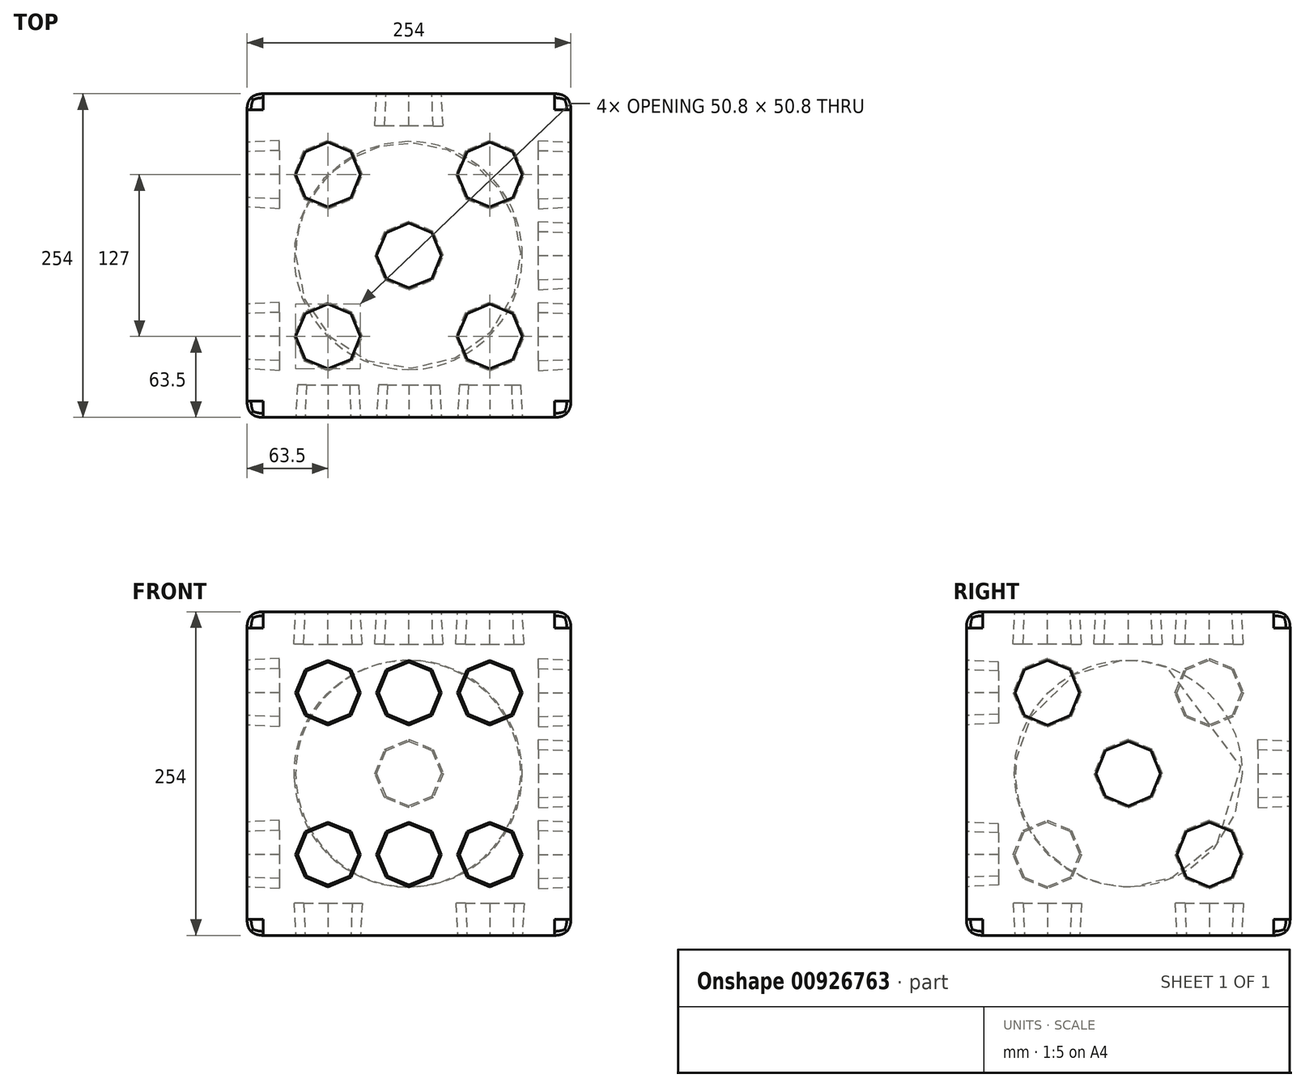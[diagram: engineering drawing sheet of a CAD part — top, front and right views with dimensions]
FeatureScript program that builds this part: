
annotation { "Feature Type Name" : "Feature", "Feature Type Description" : "" }
export const myFeature = defineFeature(function(context is Context, id is Id, definition is map)
    precondition{}
    {
        {
            var Q0;
            Q0=qCreatedBy(makeId("Front.planeOp"),FACE);
            var sketch = newSketch(context, id + "F0", { "sketchPlane" : qUnion([Q0])});
            skLineSegment(sketch, "E0.bottom", {"start": v(127, -127) * mm, "end": v(-127, -127) * mm});
            skLineSegment(sketch, "E0.top", {"start": v(127, 127) * mm, "end": v(-127, 127) * mm});
            skLineSegment(sketch, "E0.left", {"start": v(127, -127) * mm, "end": v(127, 127) * mm});
            skLineSegment(sketch, "E0.right", {"start": v(-127, -127) * mm, "end": v(-127, 127) * mm});
            skPoint(sketch, "E0.middle", {"position": v(0, 0) * mm});
            skLineSegment(sketch, "E1", {"start": v(-63.5, 127) * mm, "end": v(-63.5, -127) * mm, "construction": true});
            skLineSegment(sketch, "E2", {"start": v(0, -127) * mm, "end": v(0, 127) * mm, "construction": true});
            skLineSegment(sketch, "E3", {"start": v(63.5, 127) * mm, "end": v(63.5, -127) * mm, "construction": true});
            skLineSegment(sketch, "E4", {"start": v(-127, 63.5) * mm, "end": v(127, 63.5) * mm, "construction": true});
            skLineSegment(sketch, "E5", {"start": v(-127, 0) * mm, "end": v(127, 0) * mm, "construction": true});
            skLineSegment(sketch, "E6", {"start": v(-127, -63.5) * mm, "end": v(127, -63.5) * mm, "construction": true});
            skLineSegment(sketch, "E7.bottom", {"start": v(-38.1, 38.1) * mm, "end": v(-88.9, 38.1) * mm});
            skLineSegment(sketch, "E7.top", {"start": v(-38.1, 88.9) * mm, "end": v(-88.9, 88.9) * mm});
            skLineSegment(sketch, "E7.left", {"start": v(-38.1, 38.1) * mm, "end": v(-38.1, 88.9) * mm});
            skLineSegment(sketch, "E7.right", {"start": v(-88.9, 38.1) * mm, "end": v(-88.9, 88.9) * mm});
            skPoint(sketch, "E7.middle", {"position": v(-63.5, 63.5) * mm});
            skLineSegment(sketch, "E8.bottom", {"start": v(25.4, 38.1) * mm, "end": v(-25.4, 38.1) * mm});
            skLineSegment(sketch, "E8.top", {"start": v(25.4, 88.9) * mm, "end": v(-25.4, 88.9) * mm});
            skLineSegment(sketch, "E8.left", {"start": v(25.4, 38.1) * mm, "end": v(25.4, 88.9) * mm});
            skLineSegment(sketch, "E8.right", {"start": v(-25.4, 38.1) * mm, "end": v(-25.4, 88.9) * mm});
            skPoint(sketch, "E8.middle", {"position": v(0, 63.5) * mm});
            skLineSegment(sketch, "E9.bottom", {"start": v(88.9, 38.1) * mm, "end": v(38.1, 38.1) * mm});
            skLineSegment(sketch, "E9.top", {"start": v(88.9, 88.9) * mm, "end": v(38.1, 88.9) * mm});
            skLineSegment(sketch, "E9.left", {"start": v(88.9, 38.1) * mm, "end": v(88.9, 88.9) * mm});
            skLineSegment(sketch, "E9.right", {"start": v(38.1, 38.1) * mm, "end": v(38.1, 88.9) * mm});
            skPoint(sketch, "E9.middle", {"position": v(63.5, 63.5) * mm});
            skLineSegment(sketch, "E10.bottom", {"start": v(-38.1, -25.4) * mm, "end": v(-88.9, -25.4) * mm});
            skLineSegment(sketch, "E10.top", {"start": v(-38.1, 25.4) * mm, "end": v(-88.9, 25.4) * mm});
            skLineSegment(sketch, "E10.left", {"start": v(-38.1, -25.4) * mm, "end": v(-38.1, 25.4) * mm});
            skLineSegment(sketch, "E10.right", {"start": v(-88.9, -25.4) * mm, "end": v(-88.9, 25.4) * mm});
            skPoint(sketch, "E10.middle", {"position": v(-63.5, 0) * mm});
            skLineSegment(sketch, "E11.bottom", {"start": v(25.4, -25.4) * mm, "end": v(-25.4, -25.4) * mm});
            skLineSegment(sketch, "E11.top", {"start": v(25.4, 25.4) * mm, "end": v(-25.4, 25.4) * mm});
            skLineSegment(sketch, "E11.left", {"start": v(25.4, -25.4) * mm, "end": v(25.4, 25.4) * mm});
            skLineSegment(sketch, "E11.right", {"start": v(-25.4, -25.4) * mm, "end": v(-25.4, 25.4) * mm});
            skLineSegment(sketch, "E12.bottom", {"start": v(88.9, -25.4) * mm, "end": v(38.1, -25.4) * mm});
            skLineSegment(sketch, "E12.top", {"start": v(88.9, 25.4) * mm, "end": v(38.1, 25.4) * mm});
            skLineSegment(sketch, "E12.left", {"start": v(88.9, -25.4) * mm, "end": v(88.9, 25.4) * mm});
            skLineSegment(sketch, "E12.right", {"start": v(38.1, -25.4) * mm, "end": v(38.1, 25.4) * mm});
            skPoint(sketch, "E12.middle", {"position": v(63.5, 0) * mm});
            skLineSegment(sketch, "E13.bottom", {"start": v(-38.1, -88.9) * mm, "end": v(-88.9, -88.9) * mm});
            skLineSegment(sketch, "E13.top", {"start": v(-38.1, -38.1) * mm, "end": v(-88.9, -38.1) * mm});
            skLineSegment(sketch, "E13.left", {"start": v(-38.1, -88.9) * mm, "end": v(-38.1, -38.1) * mm});
            skLineSegment(sketch, "E13.right", {"start": v(-88.9, -88.9) * mm, "end": v(-88.9, -38.1) * mm});
            skPoint(sketch, "E13.middle", {"position": v(-63.5, -63.5) * mm});
            skLineSegment(sketch, "E14.bottom", {"start": v(25.4, -88.9) * mm, "end": v(-25.4, -88.9) * mm});
            skLineSegment(sketch, "E14.top", {"start": v(25.4, -38.1) * mm, "end": v(-25.4, -38.1) * mm});
            skLineSegment(sketch, "E14.left", {"start": v(25.4, -88.9) * mm, "end": v(25.4, -38.1) * mm});
            skLineSegment(sketch, "E14.right", {"start": v(-25.4, -88.9) * mm, "end": v(-25.4, -38.1) * mm});
            skPoint(sketch, "E14.middle", {"position": v(0, -63.5) * mm});
            skLineSegment(sketch, "E15.bottom", {"start": v(88.9, -88.9) * mm, "end": v(38.1, -88.9) * mm});
            skLineSegment(sketch, "E15.top", {"start": v(88.9, -38.1) * mm, "end": v(38.1, -38.1) * mm});
            skLineSegment(sketch, "E15.left", {"start": v(88.9, -88.9) * mm, "end": v(88.9, -38.1) * mm});
            skLineSegment(sketch, "E15.right", {"start": v(38.1, -88.9) * mm, "end": v(38.1, -38.1) * mm});
            skPoint(sketch, "E15.middle", {"position": v(63.5, -63.5) * mm});
            skCircle(sketch, "E16.cCircle", {"center": v(-63.5, 63.5) * mm, "radius": 25.4 * mm, "construction": true});
            skLineSegment(sketch, "E16.0", {"start": v(-88.9, 63.5) * mm, "end": v(-81.46, 81.46) * mm});
            skLineSegment(sketch, "E16.1", {"start": v(-81.46, 81.46) * mm, "end": v(-63.5, 88.9) * mm});
            skLineSegment(sketch, "E16.2", {"start": v(-63.5, 88.9) * mm, "end": v(-45.54, 81.46) * mm});
            skLineSegment(sketch, "E16.3", {"start": v(-45.54, 81.46) * mm, "end": v(-38.1, 63.5) * mm});
            skLineSegment(sketch, "E16.4", {"start": v(-38.1, 63.5) * mm, "end": v(-45.54, 45.54) * mm});
            skLineSegment(sketch, "E16.5", {"start": v(-45.54, 45.54) * mm, "end": v(-63.5, 38.1) * mm});
            skLineSegment(sketch, "E16.6", {"start": v(-63.5, 38.1) * mm, "end": v(-81.46, 45.54) * mm});
            skLineSegment(sketch, "E16.7", {"start": v(-81.46, 45.54) * mm, "end": v(-88.9, 63.5) * mm});
            skCircle(sketch, "E17.cCircle", {"center": v(0, 63.5) * mm, "radius": 25.4 * mm, "construction": true});
            skLineSegment(sketch, "E17.0", {"start": v(-25.4, 63.5) * mm, "end": v(-17.96, 81.46) * mm});
            skLineSegment(sketch, "E17.1", {"start": v(-17.96, 81.46) * mm, "end": v(0, 88.9) * mm});
            skLineSegment(sketch, "E17.2", {"start": v(0, 88.9) * mm, "end": v(17.96, 81.46) * mm});
            skLineSegment(sketch, "E17.3", {"start": v(17.96, 81.46) * mm, "end": v(25.4, 63.5) * mm});
            skLineSegment(sketch, "E17.4", {"start": v(25.4, 63.5) * mm, "end": v(17.96, 45.54) * mm});
            skLineSegment(sketch, "E17.5", {"start": v(17.96, 45.54) * mm, "end": v(0, 38.1) * mm});
            skLineSegment(sketch, "E17.6", {"start": v(0, 38.1) * mm, "end": v(-17.96, 45.54) * mm});
            skLineSegment(sketch, "E17.7", {"start": v(-17.96, 45.54) * mm, "end": v(-25.4, 63.5) * mm});
            skCircle(sketch, "E18.cCircle", {"center": v(63.5, 63.5) * mm, "radius": 25.4 * mm, "construction": true});
            skLineSegment(sketch, "E18.0", {"start": v(38.1, 63.5) * mm, "end": v(45.54, 81.46) * mm});
            skLineSegment(sketch, "E18.1", {"start": v(45.54, 81.46) * mm, "end": v(63.5, 88.9) * mm});
            skLineSegment(sketch, "E18.2", {"start": v(63.5, 88.9) * mm, "end": v(81.46, 81.46) * mm});
            skLineSegment(sketch, "E18.3", {"start": v(81.46, 81.46) * mm, "end": v(88.9, 63.5) * mm});
            skLineSegment(sketch, "E18.4", {"start": v(88.9, 63.5) * mm, "end": v(81.46, 45.54) * mm});
            skLineSegment(sketch, "E18.5", {"start": v(81.46, 45.54) * mm, "end": v(63.5, 38.1) * mm});
            skLineSegment(sketch, "E18.6", {"start": v(63.5, 38.1) * mm, "end": v(45.54, 45.54) * mm});
            skLineSegment(sketch, "E18.7", {"start": v(45.54, 45.54) * mm, "end": v(38.1, 63.5) * mm});
            skCircle(sketch, "E19.cCircle", {"center": v(63.5, 0) * mm, "radius": 25.4 * mm, "construction": true});
            skLineSegment(sketch, "E19.0", {"start": v(38.1, 0) * mm, "end": v(45.54, 17.96) * mm});
            skLineSegment(sketch, "E19.1", {"start": v(45.54, 17.96) * mm, "end": v(63.5, 25.4) * mm});
            skLineSegment(sketch, "E19.2", {"start": v(63.5, 25.4) * mm, "end": v(81.46, 17.96) * mm});
            skLineSegment(sketch, "E19.3", {"start": v(81.46, 17.96) * mm, "end": v(88.9, 0) * mm});
            skLineSegment(sketch, "E19.4", {"start": v(88.9, 0) * mm, "end": v(81.46, -17.96) * mm});
            skLineSegment(sketch, "E19.5", {"start": v(81.46, -17.96) * mm, "end": v(63.5, -25.4) * mm});
            skLineSegment(sketch, "E19.6", {"start": v(63.5, -25.4) * mm, "end": v(45.54, -17.96) * mm});
            skLineSegment(sketch, "E19.7", {"start": v(45.54, -17.96) * mm, "end": v(38.1, 0) * mm});
            skCircle(sketch, "E20.cCircle", {"center": v(0, 0) * mm, "radius": 25.4 * mm, "construction": true});
            skLineSegment(sketch, "E20.0", {"start": v(-25.4, 0) * mm, "end": v(-17.96, 17.96) * mm});
            skLineSegment(sketch, "E20.1", {"start": v(-17.96, 17.96) * mm, "end": v(0, 25.4) * mm});
            skLineSegment(sketch, "E20.2", {"start": v(0, 25.4) * mm, "end": v(17.96, 17.96) * mm});
            skLineSegment(sketch, "E20.3", {"start": v(17.96, 17.96) * mm, "end": v(25.4, 0) * mm});
            skLineSegment(sketch, "E20.4", {"start": v(25.4, 0) * mm, "end": v(17.96, -17.96) * mm});
            skLineSegment(sketch, "E20.5", {"start": v(17.96, -17.96) * mm, "end": v(0, -25.4) * mm});
            skLineSegment(sketch, "E20.6", {"start": v(0, -25.4) * mm, "end": v(-17.96, -17.96) * mm});
            skLineSegment(sketch, "E20.7", {"start": v(-17.96, -17.96) * mm, "end": v(-25.4, 0) * mm});
            skCircle(sketch, "E21.cCircle", {"center": v(-63.5, 0) * mm, "radius": 25.4 * mm, "construction": true});
            skLineSegment(sketch, "E21.0", {"start": v(-88.9, 0) * mm, "end": v(-81.46, 17.96) * mm});
            skLineSegment(sketch, "E21.1", {"start": v(-81.46, 17.96) * mm, "end": v(-63.5, 25.4) * mm});
            skLineSegment(sketch, "E21.2", {"start": v(-63.5, 25.4) * mm, "end": v(-45.54, 17.96) * mm});
            skLineSegment(sketch, "E21.3", {"start": v(-45.54, 17.96) * mm, "end": v(-38.1, 0) * mm});
            skLineSegment(sketch, "E21.4", {"start": v(-38.1, 0) * mm, "end": v(-45.54, -17.96) * mm});
            skLineSegment(sketch, "E21.5", {"start": v(-45.54, -17.96) * mm, "end": v(-63.5, -25.4) * mm});
            skLineSegment(sketch, "E21.6", {"start": v(-63.5, -25.4) * mm, "end": v(-81.46, -17.96) * mm});
            skLineSegment(sketch, "E21.7", {"start": v(-81.46, -17.96) * mm, "end": v(-88.9, 0) * mm});
            skCircle(sketch, "E22.cCircle", {"center": v(-63.5, -63.5) * mm, "radius": 25.4 * mm, "construction": true});
            skLineSegment(sketch, "E22.0", {"start": v(-88.9, -63.5) * mm, "end": v(-81.46, -45.54) * mm});
            skLineSegment(sketch, "E22.1", {"start": v(-81.46, -45.54) * mm, "end": v(-63.5, -38.1) * mm});
            skLineSegment(sketch, "E22.2", {"start": v(-63.5, -38.1) * mm, "end": v(-45.54, -45.54) * mm});
            skLineSegment(sketch, "E22.3", {"start": v(-45.54, -45.54) * mm, "end": v(-38.1, -63.5) * mm});
            skLineSegment(sketch, "E22.4", {"start": v(-38.1, -63.5) * mm, "end": v(-45.54, -81.46) * mm});
            skLineSegment(sketch, "E22.5", {"start": v(-45.54, -81.46) * mm, "end": v(-63.5, -88.9) * mm});
            skLineSegment(sketch, "E22.6", {"start": v(-63.5, -88.9) * mm, "end": v(-81.46, -81.46) * mm});
            skLineSegment(sketch, "E22.7", {"start": v(-81.46, -81.46) * mm, "end": v(-88.9, -63.5) * mm});
            skCircle(sketch, "E23.cCircle", {"center": v(0, -63.5) * mm, "radius": 25.4 * mm, "construction": true});
            skLineSegment(sketch, "E23.0", {"start": v(-25.4, -63.5) * mm, "end": v(-17.96, -45.54) * mm});
            skLineSegment(sketch, "E23.1", {"start": v(-17.96, -45.54) * mm, "end": v(0, -38.1) * mm});
            skLineSegment(sketch, "E23.2", {"start": v(0, -38.1) * mm, "end": v(17.96, -45.54) * mm});
            skLineSegment(sketch, "E23.3", {"start": v(17.96, -45.54) * mm, "end": v(25.4, -63.5) * mm});
            skLineSegment(sketch, "E23.4", {"start": v(25.4, -63.5) * mm, "end": v(17.96, -81.46) * mm});
            skLineSegment(sketch, "E23.5", {"start": v(17.96, -81.46) * mm, "end": v(0, -88.9) * mm});
            skLineSegment(sketch, "E23.6", {"start": v(0, -88.9) * mm, "end": v(-17.96, -81.46) * mm});
            skLineSegment(sketch, "E23.7", {"start": v(-17.96, -81.46) * mm, "end": v(-25.4, -63.5) * mm});
            skCircle(sketch, "E24.cCircle", {"center": v(63.5, -63.5) * mm, "radius": 25.4 * mm, "construction": true});
            skLineSegment(sketch, "E24.0", {"start": v(38.1, -63.5) * mm, "end": v(45.54, -45.54) * mm});
            skLineSegment(sketch, "E24.1", {"start": v(45.54, -45.54) * mm, "end": v(63.5, -38.1) * mm});
            skLineSegment(sketch, "E24.2", {"start": v(63.5, -38.1) * mm, "end": v(81.46, -45.54) * mm});
            skLineSegment(sketch, "E24.3", {"start": v(81.46, -45.54) * mm, "end": v(88.9, -63.5) * mm});
            skLineSegment(sketch, "E24.4", {"start": v(88.9, -63.5) * mm, "end": v(81.46, -81.46) * mm});
            skLineSegment(sketch, "E24.5", {"start": v(81.46, -81.46) * mm, "end": v(63.5, -88.9) * mm});
            skLineSegment(sketch, "E24.6", {"start": v(63.5, -88.9) * mm, "end": v(45.54, -81.46) * mm});
            skLineSegment(sketch, "E24.7", {"start": v(45.54, -81.46) * mm, "end": v(38.1, -63.5) * mm});
            skSolve(sketch);
        }
        {
            var Q0;
            Q0=qCreatedBy(makeId("Front.planeOp"),FACE);
            var sketch = newSketch(context, id + "F1", { "sketchPlane" : qUnion([Q0])});
            skLineSegment(sketch, "E25.bottom", {"start": v(-127, 127) * mm, "end": v(127, 127) * mm});
            skLineSegment(sketch, "E25.top", {"start": v(-127, -127) * mm, "end": v(127, -127) * mm});
            skLineSegment(sketch, "E25.left", {"start": v(-127, 127) * mm, "end": v(-127, -127) * mm});
            skLineSegment(sketch, "E25.right", {"start": v(127, 127) * mm, "end": v(127, -127) * mm});
            skPoint(sketch, "E25.middle", {"position": v(0, 0) * mm});
            skSolve(sketch);
        }
        {
            var Q0;
            Q0=makeQuery(id+"F1.imprint","IMPRINT",FACE,{"disambiguationData":[TD([[makeQuery(id+"F1.imprint","IMPRINT",EDGE,{"derivedFrom":sQuery(id+"F1.wireOp",EDGE,"E25.bottom")}),-1.0]])]});
            extrude(context, id + "F2", {"entities" : qUnion([Q0]), "oppositeDirection" : true, "depth" : 254 * mm, "offsetDistance" : 25.4 * mm});
        }
        {
            var Q0;
            Q0=makeQuery(id+"F2.opExtrude","SWEPT_FACE",FACE,{"disambiguationData":[OSD([sQuery(id+"F1.wireOp",EDGE,"E25.left")])]});
            var sketch = newSketch(context, id + "F3", { "sketchPlane" : qUnion([Q0])});
            skLineSegment(sketch, "E26.bottom", {"start": v(0, -127) * mm, "end": v(-254, -127) * mm});
            skLineSegment(sketch, "E26.top", {"start": v(0, 127) * mm, "end": v(-254, 127) * mm});
            skLineSegment(sketch, "E26.left", {"start": v(0, -127) * mm, "end": v(0, 127) * mm});
            skLineSegment(sketch, "E26.right", {"start": v(-254, -127) * mm, "end": v(-254, 127) * mm});
            skPoint(sketch, "E26.middle", {"position": v(-127, 0) * mm});
            skLineSegment(sketch, "E27", {"start": v(-190.5, 127) * mm, "end": v(-190.5, -127) * mm, "construction": true});
            skLineSegment(sketch, "E28", {"start": v(-127, -127) * mm, "end": v(-127, 127) * mm, "construction": true});
            skLineSegment(sketch, "E29", {"start": v(-63.5, 127) * mm, "end": v(-63.5, -127) * mm, "construction": true});
            skLineSegment(sketch, "E30", {"start": v(-254, 63.5) * mm, "end": v(0, 63.5) * mm, "construction": true});
            skLineSegment(sketch, "E31", {"start": v(-254, 0) * mm, "end": v(0, 0) * mm, "construction": true});
            skLineSegment(sketch, "E32", {"start": v(-254, -63.5) * mm, "end": v(0, -63.5) * mm, "construction": true});
            skLineSegment(sketch, "E33.bottom", {"start": v(-165.1, 38.1) * mm, "end": v(-215.9, 38.1) * mm});
            skLineSegment(sketch, "E33.top", {"start": v(-165.1, 88.9) * mm, "end": v(-215.9, 88.9) * mm});
            skLineSegment(sketch, "E33.left", {"start": v(-165.1, 38.1) * mm, "end": v(-165.1, 88.9) * mm});
            skLineSegment(sketch, "E33.right", {"start": v(-215.9, 38.1) * mm, "end": v(-215.9, 88.9) * mm});
            skPoint(sketch, "E33.middle", {"position": v(-190.5, 63.5) * mm});
            skLineSegment(sketch, "E34.bottom", {"start": v(-101.6, 38.1) * mm, "end": v(-152.4, 38.1) * mm});
            skLineSegment(sketch, "E34.top", {"start": v(-101.6, 88.9) * mm, "end": v(-152.4, 88.9) * mm});
            skLineSegment(sketch, "E34.left", {"start": v(-101.6, 38.1) * mm, "end": v(-101.6, 88.9) * mm});
            skLineSegment(sketch, "E34.right", {"start": v(-152.4, 38.1) * mm, "end": v(-152.4, 88.9) * mm});
            skPoint(sketch, "E34.middle", {"position": v(-127, 63.5) * mm});
            skLineSegment(sketch, "E35.bottom", {"start": v(-38.1, 38.1) * mm, "end": v(-88.9, 38.1) * mm});
            skLineSegment(sketch, "E35.top", {"start": v(-38.1, 88.9) * mm, "end": v(-88.9, 88.9) * mm});
            skLineSegment(sketch, "E35.left", {"start": v(-38.1, 38.1) * mm, "end": v(-38.1, 88.9) * mm});
            skLineSegment(sketch, "E35.right", {"start": v(-88.9, 38.1) * mm, "end": v(-88.9, 88.9) * mm});
            skPoint(sketch, "E35.middle", {"position": v(-63.5, 63.5) * mm});
            skLineSegment(sketch, "E36.bottom", {"start": v(-165.1, -25.4) * mm, "end": v(-215.9, -25.4) * mm});
            skLineSegment(sketch, "E36.top", {"start": v(-165.1, 25.4) * mm, "end": v(-215.9, 25.4) * mm});
            skLineSegment(sketch, "E36.left", {"start": v(-165.1, -25.4) * mm, "end": v(-165.1, 25.4) * mm});
            skLineSegment(sketch, "E36.right", {"start": v(-215.9, -25.4) * mm, "end": v(-215.9, 25.4) * mm});
            skPoint(sketch, "E36.middle", {"position": v(-190.5, 0) * mm});
            skLineSegment(sketch, "E37.bottom", {"start": v(-101.6, -25.4) * mm, "end": v(-152.4, -25.4) * mm});
            skLineSegment(sketch, "E37.top", {"start": v(-101.6, 25.4) * mm, "end": v(-152.4, 25.4) * mm});
            skLineSegment(sketch, "E37.left", {"start": v(-101.6, -25.4) * mm, "end": v(-101.6, 25.4) * mm});
            skLineSegment(sketch, "E37.right", {"start": v(-152.4, -25.4) * mm, "end": v(-152.4, 25.4) * mm});
            skLineSegment(sketch, "E38.bottom", {"start": v(-38.1, -25.4) * mm, "end": v(-88.9, -25.4) * mm});
            skLineSegment(sketch, "E38.top", {"start": v(-38.1, 25.4) * mm, "end": v(-88.9, 25.4) * mm});
            skLineSegment(sketch, "E38.left", {"start": v(-38.1, -25.4) * mm, "end": v(-38.1, 25.4) * mm});
            skLineSegment(sketch, "E38.right", {"start": v(-88.9, -25.4) * mm, "end": v(-88.9, 25.4) * mm});
            skPoint(sketch, "E38.middle", {"position": v(-63.5, 0) * mm});
            skLineSegment(sketch, "E39.bottom", {"start": v(-165.1, -88.9) * mm, "end": v(-215.9, -88.9) * mm});
            skLineSegment(sketch, "E39.top", {"start": v(-165.1, -38.1) * mm, "end": v(-215.9, -38.1) * mm});
            skLineSegment(sketch, "E39.left", {"start": v(-165.1, -88.9) * mm, "end": v(-165.1, -38.1) * mm});
            skLineSegment(sketch, "E39.right", {"start": v(-215.9, -88.9) * mm, "end": v(-215.9, -38.1) * mm});
            skPoint(sketch, "E39.middle", {"position": v(-190.5, -63.5) * mm});
            skLineSegment(sketch, "E40.bottom", {"start": v(-101.6, -88.9) * mm, "end": v(-152.4, -88.9) * mm});
            skLineSegment(sketch, "E40.top", {"start": v(-101.6, -38.1) * mm, "end": v(-152.4, -38.1) * mm});
            skLineSegment(sketch, "E40.left", {"start": v(-101.6, -88.9) * mm, "end": v(-101.6, -38.1) * mm});
            skLineSegment(sketch, "E40.right", {"start": v(-152.4, -88.9) * mm, "end": v(-152.4, -38.1) * mm});
            skPoint(sketch, "E40.middle", {"position": v(-127, -63.5) * mm});
            skLineSegment(sketch, "E41.bottom", {"start": v(-38.1, -88.9) * mm, "end": v(-88.9, -88.9) * mm});
            skLineSegment(sketch, "E41.top", {"start": v(-38.1, -38.1) * mm, "end": v(-88.9, -38.1) * mm});
            skLineSegment(sketch, "E41.left", {"start": v(-38.1, -88.9) * mm, "end": v(-38.1, -38.1) * mm});
            skLineSegment(sketch, "E41.right", {"start": v(-88.9, -88.9) * mm, "end": v(-88.9, -38.1) * mm});
            skPoint(sketch, "E41.middle", {"position": v(-63.5, -63.5) * mm});
            skCircle(sketch, "E42.cCircle", {"center": v(-190.5, 63.5) * mm, "radius": 25.4 * mm, "construction": true});
            skLineSegment(sketch, "E42.0", {"start": v(-215.9, 63.5) * mm, "end": v(-208.46, 81.46) * mm});
            skLineSegment(sketch, "E42.1", {"start": v(-208.46, 81.46) * mm, "end": v(-190.5, 88.9) * mm});
            skLineSegment(sketch, "E42.2", {"start": v(-190.5, 88.9) * mm, "end": v(-172.54, 81.46) * mm});
            skLineSegment(sketch, "E42.3", {"start": v(-172.54, 81.46) * mm, "end": v(-165.1, 63.5) * mm});
            skLineSegment(sketch, "E42.4", {"start": v(-165.1, 63.5) * mm, "end": v(-172.54, 45.54) * mm});
            skLineSegment(sketch, "E42.5", {"start": v(-172.54, 45.54) * mm, "end": v(-190.5, 38.1) * mm});
            skLineSegment(sketch, "E42.6", {"start": v(-190.5, 38.1) * mm, "end": v(-208.46, 45.54) * mm});
            skLineSegment(sketch, "E42.7", {"start": v(-208.46, 45.54) * mm, "end": v(-215.9, 63.5) * mm});
            skCircle(sketch, "E43.cCircle", {"center": v(-127, 63.5) * mm, "radius": 25.4 * mm, "construction": true});
            skLineSegment(sketch, "E43.0", {"start": v(-152.4, 63.5) * mm, "end": v(-144.96, 81.46) * mm});
            skLineSegment(sketch, "E43.1", {"start": v(-144.96, 81.46) * mm, "end": v(-127, 88.9) * mm});
            skLineSegment(sketch, "E43.2", {"start": v(-127, 88.9) * mm, "end": v(-109.04, 81.46) * mm});
            skLineSegment(sketch, "E43.3", {"start": v(-109.04, 81.46) * mm, "end": v(-101.6, 63.5) * mm});
            skLineSegment(sketch, "E43.4", {"start": v(-101.6, 63.5) * mm, "end": v(-109.04, 45.54) * mm});
            skLineSegment(sketch, "E43.5", {"start": v(-109.04, 45.54) * mm, "end": v(-127, 38.1) * mm});
            skLineSegment(sketch, "E43.6", {"start": v(-127, 38.1) * mm, "end": v(-144.96, 45.54) * mm});
            skLineSegment(sketch, "E43.7", {"start": v(-144.96, 45.54) * mm, "end": v(-152.4, 63.5) * mm});
            skCircle(sketch, "E44.cCircle", {"center": v(-63.5, 63.5) * mm, "radius": 25.4 * mm, "construction": true});
            skLineSegment(sketch, "E44.0", {"start": v(-88.9, 63.5) * mm, "end": v(-81.46, 81.46) * mm});
            skLineSegment(sketch, "E44.1", {"start": v(-81.46, 81.46) * mm, "end": v(-63.5, 88.9) * mm});
            skLineSegment(sketch, "E44.2", {"start": v(-63.5, 88.9) * mm, "end": v(-45.54, 81.46) * mm});
            skLineSegment(sketch, "E44.3", {"start": v(-45.54, 81.46) * mm, "end": v(-38.1, 63.5) * mm});
            skLineSegment(sketch, "E44.4", {"start": v(-38.1, 63.5) * mm, "end": v(-45.54, 45.54) * mm});
            skLineSegment(sketch, "E44.5", {"start": v(-45.54, 45.54) * mm, "end": v(-63.5, 38.1) * mm});
            skLineSegment(sketch, "E44.6", {"start": v(-63.5, 38.1) * mm, "end": v(-81.46, 45.54) * mm});
            skLineSegment(sketch, "E44.7", {"start": v(-81.46, 45.54) * mm, "end": v(-88.9, 63.5) * mm});
            skCircle(sketch, "E45.cCircle", {"center": v(-63.5, 0) * mm, "radius": 25.4 * mm, "construction": true});
            skLineSegment(sketch, "E45.0", {"start": v(-88.9, 0) * mm, "end": v(-81.46, 17.96) * mm});
            skLineSegment(sketch, "E45.1", {"start": v(-81.46, 17.96) * mm, "end": v(-63.5, 25.4) * mm});
            skLineSegment(sketch, "E45.2", {"start": v(-63.5, 25.4) * mm, "end": v(-45.54, 17.96) * mm});
            skLineSegment(sketch, "E45.3", {"start": v(-45.54, 17.96) * mm, "end": v(-38.1, 0) * mm});
            skLineSegment(sketch, "E45.4", {"start": v(-38.1, 0) * mm, "end": v(-45.54, -17.96) * mm});
            skLineSegment(sketch, "E45.5", {"start": v(-45.54, -17.96) * mm, "end": v(-63.5, -25.4) * mm});
            skLineSegment(sketch, "E45.6", {"start": v(-63.5, -25.4) * mm, "end": v(-81.46, -17.96) * mm});
            skLineSegment(sketch, "E45.7", {"start": v(-81.46, -17.96) * mm, "end": v(-88.9, 0) * mm});
            skCircle(sketch, "E46.cCircle", {"center": v(-127, 0) * mm, "radius": 25.4 * mm, "construction": true});
            skLineSegment(sketch, "E46.0", {"start": v(-152.4, 0) * mm, "end": v(-144.96, 17.96) * mm});
            skLineSegment(sketch, "E46.1", {"start": v(-144.96, 17.96) * mm, "end": v(-127, 25.4) * mm});
            skLineSegment(sketch, "E46.2", {"start": v(-127, 25.4) * mm, "end": v(-109.04, 17.96) * mm});
            skLineSegment(sketch, "E46.3", {"start": v(-109.04, 17.96) * mm, "end": v(-101.6, 0) * mm});
            skLineSegment(sketch, "E46.4", {"start": v(-101.6, 0) * mm, "end": v(-109.04, -17.96) * mm});
            skLineSegment(sketch, "E46.5", {"start": v(-109.04, -17.96) * mm, "end": v(-127, -25.4) * mm});
            skLineSegment(sketch, "E46.6", {"start": v(-127, -25.4) * mm, "end": v(-144.96, -17.96) * mm});
            skLineSegment(sketch, "E46.7", {"start": v(-144.96, -17.96) * mm, "end": v(-152.4, 0) * mm});
            skCircle(sketch, "E47.cCircle", {"center": v(-190.5, 0) * mm, "radius": 25.4 * mm, "construction": true});
            skLineSegment(sketch, "E47.0", {"start": v(-215.9, 0) * mm, "end": v(-208.46, 17.96) * mm});
            skLineSegment(sketch, "E47.1", {"start": v(-208.46, 17.96) * mm, "end": v(-190.5, 25.4) * mm});
            skLineSegment(sketch, "E47.2", {"start": v(-190.5, 25.4) * mm, "end": v(-172.54, 17.96) * mm});
            skLineSegment(sketch, "E47.3", {"start": v(-172.54, 17.96) * mm, "end": v(-165.1, 0) * mm});
            skLineSegment(sketch, "E47.4", {"start": v(-165.1, 0) * mm, "end": v(-172.54, -17.96) * mm});
            skLineSegment(sketch, "E47.5", {"start": v(-172.54, -17.96) * mm, "end": v(-190.5, -25.4) * mm});
            skLineSegment(sketch, "E47.6", {"start": v(-190.5, -25.4) * mm, "end": v(-208.46, -17.96) * mm});
            skLineSegment(sketch, "E47.7", {"start": v(-208.46, -17.96) * mm, "end": v(-215.9, 0) * mm});
            skCircle(sketch, "E48.cCircle", {"center": v(-190.5, -63.5) * mm, "radius": 25.4 * mm, "construction": true});
            skLineSegment(sketch, "E48.0", {"start": v(-215.9, -63.5) * mm, "end": v(-208.46, -45.54) * mm});
            skLineSegment(sketch, "E48.1", {"start": v(-208.46, -45.54) * mm, "end": v(-190.5, -38.1) * mm});
            skLineSegment(sketch, "E48.2", {"start": v(-190.5, -38.1) * mm, "end": v(-172.54, -45.54) * mm});
            skLineSegment(sketch, "E48.3", {"start": v(-172.54, -45.54) * mm, "end": v(-165.1, -63.5) * mm});
            skLineSegment(sketch, "E48.4", {"start": v(-165.1, -63.5) * mm, "end": v(-172.54, -81.46) * mm});
            skLineSegment(sketch, "E48.5", {"start": v(-172.54, -81.46) * mm, "end": v(-190.5, -88.9) * mm});
            skLineSegment(sketch, "E48.6", {"start": v(-190.5, -88.9) * mm, "end": v(-208.46, -81.46) * mm});
            skLineSegment(sketch, "E48.7", {"start": v(-208.46, -81.46) * mm, "end": v(-215.9, -63.5) * mm});
            skCircle(sketch, "E49.cCircle", {"center": v(-127, -63.5) * mm, "radius": 25.4 * mm, "construction": true});
            skLineSegment(sketch, "E49.0", {"start": v(-152.4, -63.5) * mm, "end": v(-144.96, -45.54) * mm});
            skLineSegment(sketch, "E49.1", {"start": v(-144.96, -45.54) * mm, "end": v(-127, -38.1) * mm});
            skLineSegment(sketch, "E49.2", {"start": v(-127, -38.1) * mm, "end": v(-109.04, -45.54) * mm});
            skLineSegment(sketch, "E49.3", {"start": v(-109.04, -45.54) * mm, "end": v(-101.6, -63.5) * mm});
            skLineSegment(sketch, "E49.4", {"start": v(-101.6, -63.5) * mm, "end": v(-109.04, -81.46) * mm});
            skLineSegment(sketch, "E49.5", {"start": v(-109.04, -81.46) * mm, "end": v(-127, -88.9) * mm});
            skLineSegment(sketch, "E49.6", {"start": v(-127, -88.9) * mm, "end": v(-144.96, -81.46) * mm});
            skLineSegment(sketch, "E49.7", {"start": v(-144.96, -81.46) * mm, "end": v(-152.4, -63.5) * mm});
            skCircle(sketch, "E50.cCircle", {"center": v(-63.5, -63.5) * mm, "radius": 25.4 * mm, "construction": true});
            skLineSegment(sketch, "E50.0", {"start": v(-88.9, -63.5) * mm, "end": v(-81.46, -45.54) * mm});
            skLineSegment(sketch, "E50.1", {"start": v(-81.46, -45.54) * mm, "end": v(-63.5, -38.1) * mm});
            skLineSegment(sketch, "E50.2", {"start": v(-63.5, -38.1) * mm, "end": v(-45.54, -45.54) * mm});
            skLineSegment(sketch, "E50.3", {"start": v(-45.54, -45.54) * mm, "end": v(-38.1, -63.5) * mm});
            skLineSegment(sketch, "E50.4", {"start": v(-38.1, -63.5) * mm, "end": v(-45.54, -81.46) * mm});
            skLineSegment(sketch, "E50.5", {"start": v(-45.54, -81.46) * mm, "end": v(-63.5, -88.9) * mm});
            skLineSegment(sketch, "E50.6", {"start": v(-63.5, -88.9) * mm, "end": v(-81.46, -81.46) * mm});
            skLineSegment(sketch, "E50.7", {"start": v(-81.46, -81.46) * mm, "end": v(-88.9, -63.5) * mm});
            skSolve(sketch);
        }
        {
            var Q0;
            Q0=makeQuery(id+"F2.opExtrude","CAP_FACE",FACE,{"disambiguationData":[OSD([sQuery(id+"F1.wireOp",EDGE,"E25.bottom"),sQuery(id+"F1.wireOp",EDGE,"E25.top"),sQuery(id+"F1.wireOp",EDGE,"E25.left"),sQuery(id+"F1.wireOp",EDGE,"E25.right")])],"isStart":false});
            var sketch = newSketch(context, id + "F4", { "sketchPlane" : qUnion([Q0])});
            skLineSegment(sketch, "E51.bottom", {"start": v(127, -127) * mm, "end": v(-127, -127) * mm});
            skLineSegment(sketch, "E51.top", {"start": v(127, 127) * mm, "end": v(-127, 127) * mm});
            skLineSegment(sketch, "E51.left", {"start": v(127, -127) * mm, "end": v(127, 127) * mm});
            skLineSegment(sketch, "E51.right", {"start": v(-127, -127) * mm, "end": v(-127, 127) * mm});
            skPoint(sketch, "E51.middle", {"position": v(0, 0) * mm});
            skLineSegment(sketch, "E52", {"start": v(-63.5, 127) * mm, "end": v(-63.5, -127) * mm, "construction": true});
            skLineSegment(sketch, "E53", {"start": v(0, -127) * mm, "end": v(0, 127) * mm, "construction": true});
            skLineSegment(sketch, "E54", {"start": v(63.5, 127) * mm, "end": v(63.5, -127) * mm, "construction": true});
            skLineSegment(sketch, "E55", {"start": v(-127, 63.5) * mm, "end": v(127, 63.5) * mm, "construction": true});
            skLineSegment(sketch, "E56", {"start": v(-127, 0) * mm, "end": v(127, 0) * mm, "construction": true});
            skLineSegment(sketch, "E57", {"start": v(-127, -63.5) * mm, "end": v(127, -63.5) * mm, "construction": true});
            skLineSegment(sketch, "E58.bottom", {"start": v(-38.1, 38.1) * mm, "end": v(-88.9, 38.1) * mm});
            skLineSegment(sketch, "E58.top", {"start": v(-38.1, 88.9) * mm, "end": v(-88.9, 88.9) * mm});
            skLineSegment(sketch, "E58.left", {"start": v(-38.1, 38.1) * mm, "end": v(-38.1, 88.9) * mm});
            skLineSegment(sketch, "E58.right", {"start": v(-88.9, 38.1) * mm, "end": v(-88.9, 88.9) * mm});
            skPoint(sketch, "E58.middle", {"position": v(-63.5, 63.5) * mm});
            skLineSegment(sketch, "E59.bottom", {"start": v(25.4, 38.1) * mm, "end": v(-25.4, 38.1) * mm});
            skLineSegment(sketch, "E59.top", {"start": v(25.4, 88.9) * mm, "end": v(-25.4, 88.9) * mm});
            skLineSegment(sketch, "E59.left", {"start": v(25.4, 38.1) * mm, "end": v(25.4, 88.9) * mm});
            skLineSegment(sketch, "E59.right", {"start": v(-25.4, 38.1) * mm, "end": v(-25.4, 88.9) * mm});
            skPoint(sketch, "E59.middle", {"position": v(0, 63.5) * mm});
            skLineSegment(sketch, "E60.bottom", {"start": v(88.9, 38.1) * mm, "end": v(38.1, 38.1) * mm});
            skLineSegment(sketch, "E60.top", {"start": v(88.9, 88.9) * mm, "end": v(38.1, 88.9) * mm});
            skLineSegment(sketch, "E60.left", {"start": v(88.9, 38.1) * mm, "end": v(88.9, 88.9) * mm});
            skLineSegment(sketch, "E60.right", {"start": v(38.1, 38.1) * mm, "end": v(38.1, 88.9) * mm});
            skPoint(sketch, "E60.middle", {"position": v(63.5, 63.5) * mm});
            skLineSegment(sketch, "E61.bottom", {"start": v(-38.1, -25.4) * mm, "end": v(-88.9, -25.4) * mm});
            skLineSegment(sketch, "E61.top", {"start": v(-38.1, 25.4) * mm, "end": v(-88.9, 25.4) * mm});
            skLineSegment(sketch, "E61.left", {"start": v(-38.1, -25.4) * mm, "end": v(-38.1, 25.4) * mm});
            skLineSegment(sketch, "E61.right", {"start": v(-88.9, -25.4) * mm, "end": v(-88.9, 25.4) * mm});
            skPoint(sketch, "E61.middle", {"position": v(-63.5, 0) * mm});
            skLineSegment(sketch, "E62.bottom", {"start": v(25.4, -25.4) * mm, "end": v(-25.4, -25.4) * mm});
            skLineSegment(sketch, "E62.top", {"start": v(25.4, 25.4) * mm, "end": v(-25.4, 25.4) * mm});
            skLineSegment(sketch, "E62.left", {"start": v(25.4, -25.4) * mm, "end": v(25.4, 25.4) * mm});
            skLineSegment(sketch, "E62.right", {"start": v(-25.4, -25.4) * mm, "end": v(-25.4, 25.4) * mm});
            skLineSegment(sketch, "E63.bottom", {"start": v(88.9, -25.4) * mm, "end": v(38.1, -25.4) * mm});
            skLineSegment(sketch, "E63.top", {"start": v(88.9, 25.4) * mm, "end": v(38.1, 25.4) * mm});
            skLineSegment(sketch, "E63.left", {"start": v(88.9, -25.4) * mm, "end": v(88.9, 25.4) * mm});
            skLineSegment(sketch, "E63.right", {"start": v(38.1, -25.4) * mm, "end": v(38.1, 25.4) * mm});
            skPoint(sketch, "E63.middle", {"position": v(63.5, 0) * mm});
            skLineSegment(sketch, "E64.bottom", {"start": v(-38.1, -88.9) * mm, "end": v(-88.9, -88.9) * mm});
            skLineSegment(sketch, "E64.top", {"start": v(-38.1, -38.1) * mm, "end": v(-88.9, -38.1) * mm});
            skLineSegment(sketch, "E64.left", {"start": v(-38.1, -88.9) * mm, "end": v(-38.1, -38.1) * mm});
            skLineSegment(sketch, "E64.right", {"start": v(-88.9, -88.9) * mm, "end": v(-88.9, -38.1) * mm});
            skPoint(sketch, "E64.middle", {"position": v(-63.5, -63.5) * mm});
            skLineSegment(sketch, "E65.bottom", {"start": v(25.4, -88.9) * mm, "end": v(-25.4, -88.9) * mm});
            skLineSegment(sketch, "E65.top", {"start": v(25.4, -38.1) * mm, "end": v(-25.4, -38.1) * mm});
            skLineSegment(sketch, "E65.left", {"start": v(25.4, -88.9) * mm, "end": v(25.4, -38.1) * mm});
            skLineSegment(sketch, "E65.right", {"start": v(-25.4, -88.9) * mm, "end": v(-25.4, -38.1) * mm});
            skPoint(sketch, "E65.middle", {"position": v(0, -63.5) * mm});
            skLineSegment(sketch, "E66.bottom", {"start": v(88.9, -88.9) * mm, "end": v(38.1, -88.9) * mm});
            skLineSegment(sketch, "E66.top", {"start": v(88.9, -38.1) * mm, "end": v(38.1, -38.1) * mm});
            skLineSegment(sketch, "E66.left", {"start": v(88.9, -88.9) * mm, "end": v(88.9, -38.1) * mm});
            skLineSegment(sketch, "E66.right", {"start": v(38.1, -88.9) * mm, "end": v(38.1, -38.1) * mm});
            skPoint(sketch, "E66.middle", {"position": v(63.5, -63.5) * mm});
            skCircle(sketch, "E67.cCircle", {"center": v(-63.5, 63.5) * mm, "radius": 25.4 * mm, "construction": true});
            skLineSegment(sketch, "E67.0", {"start": v(-88.9, 63.5) * mm, "end": v(-81.46, 81.46) * mm});
            skLineSegment(sketch, "E67.1", {"start": v(-81.46, 81.46) * mm, "end": v(-63.5, 88.9) * mm});
            skLineSegment(sketch, "E67.2", {"start": v(-63.5, 88.9) * mm, "end": v(-45.54, 81.46) * mm});
            skLineSegment(sketch, "E67.3", {"start": v(-45.54, 81.46) * mm, "end": v(-38.1, 63.5) * mm});
            skLineSegment(sketch, "E67.4", {"start": v(-38.1, 63.5) * mm, "end": v(-45.54, 45.54) * mm});
            skLineSegment(sketch, "E67.5", {"start": v(-45.54, 45.54) * mm, "end": v(-63.5, 38.1) * mm});
            skLineSegment(sketch, "E67.6", {"start": v(-63.5, 38.1) * mm, "end": v(-81.46, 45.54) * mm});
            skLineSegment(sketch, "E67.7", {"start": v(-81.46, 45.54) * mm, "end": v(-88.9, 63.5) * mm});
            skCircle(sketch, "E68.cCircle", {"center": v(0, 63.5) * mm, "radius": 25.4 * mm, "construction": true});
            skLineSegment(sketch, "E68.0", {"start": v(-25.4, 63.5) * mm, "end": v(-17.96, 81.46) * mm});
            skLineSegment(sketch, "E68.1", {"start": v(-17.96, 81.46) * mm, "end": v(0, 88.9) * mm});
            skLineSegment(sketch, "E68.2", {"start": v(0, 88.9) * mm, "end": v(17.96, 81.46) * mm});
            skLineSegment(sketch, "E68.3", {"start": v(17.96, 81.46) * mm, "end": v(25.4, 63.5) * mm});
            skLineSegment(sketch, "E68.4", {"start": v(25.4, 63.5) * mm, "end": v(17.96, 45.54) * mm});
            skLineSegment(sketch, "E68.5", {"start": v(17.96, 45.54) * mm, "end": v(0, 38.1) * mm});
            skLineSegment(sketch, "E68.6", {"start": v(0, 38.1) * mm, "end": v(-17.96, 45.54) * mm});
            skLineSegment(sketch, "E68.7", {"start": v(-17.96, 45.54) * mm, "end": v(-25.4, 63.5) * mm});
            skCircle(sketch, "E69.cCircle", {"center": v(63.5, 63.5) * mm, "radius": 25.4 * mm, "construction": true});
            skLineSegment(sketch, "E69.0", {"start": v(38.1, 63.5) * mm, "end": v(45.54, 81.46) * mm});
            skLineSegment(sketch, "E69.1", {"start": v(45.54, 81.46) * mm, "end": v(63.5, 88.9) * mm});
            skLineSegment(sketch, "E69.2", {"start": v(63.5, 88.9) * mm, "end": v(81.46, 81.46) * mm});
            skLineSegment(sketch, "E69.3", {"start": v(81.46, 81.46) * mm, "end": v(88.9, 63.5) * mm});
            skLineSegment(sketch, "E69.4", {"start": v(88.9, 63.5) * mm, "end": v(81.46, 45.54) * mm});
            skLineSegment(sketch, "E69.5", {"start": v(81.46, 45.54) * mm, "end": v(63.5, 38.1) * mm});
            skLineSegment(sketch, "E69.6", {"start": v(63.5, 38.1) * mm, "end": v(45.54, 45.54) * mm});
            skLineSegment(sketch, "E69.7", {"start": v(45.54, 45.54) * mm, "end": v(38.1, 63.5) * mm});
            skCircle(sketch, "E70.cCircle", {"center": v(63.5, 0) * mm, "radius": 25.4 * mm, "construction": true});
            skLineSegment(sketch, "E70.0", {"start": v(38.1, 0) * mm, "end": v(45.54, 17.96) * mm});
            skLineSegment(sketch, "E70.1", {"start": v(45.54, 17.96) * mm, "end": v(63.5, 25.4) * mm});
            skLineSegment(sketch, "E70.2", {"start": v(63.5, 25.4) * mm, "end": v(81.46, 17.96) * mm});
            skLineSegment(sketch, "E70.3", {"start": v(81.46, 17.96) * mm, "end": v(88.9, 0) * mm});
            skLineSegment(sketch, "E70.4", {"start": v(88.9, 0) * mm, "end": v(81.46, -17.96) * mm});
            skLineSegment(sketch, "E70.5", {"start": v(81.46, -17.96) * mm, "end": v(63.5, -25.4) * mm});
            skLineSegment(sketch, "E70.6", {"start": v(63.5, -25.4) * mm, "end": v(45.54, -17.96) * mm});
            skLineSegment(sketch, "E70.7", {"start": v(45.54, -17.96) * mm, "end": v(38.1, 0) * mm});
            skCircle(sketch, "E71.cCircle", {"center": v(0, 0) * mm, "radius": 25.4 * mm, "construction": true});
            skLineSegment(sketch, "E71.0", {"start": v(-25.4, 0) * mm, "end": v(-17.96, 17.96) * mm});
            skLineSegment(sketch, "E71.1", {"start": v(-17.96, 17.96) * mm, "end": v(0, 25.4) * mm});
            skLineSegment(sketch, "E71.2", {"start": v(0, 25.4) * mm, "end": v(17.96, 17.96) * mm});
            skLineSegment(sketch, "E71.3", {"start": v(17.96, 17.96) * mm, "end": v(25.4, 0) * mm});
            skLineSegment(sketch, "E71.4", {"start": v(25.4, 0) * mm, "end": v(17.96, -17.96) * mm});
            skLineSegment(sketch, "E71.5", {"start": v(17.96, -17.96) * mm, "end": v(0, -25.4) * mm});
            skLineSegment(sketch, "E71.6", {"start": v(0, -25.4) * mm, "end": v(-17.96, -17.96) * mm});
            skLineSegment(sketch, "E71.7", {"start": v(-17.96, -17.96) * mm, "end": v(-25.4, 0) * mm});
            skCircle(sketch, "E72.cCircle", {"center": v(-63.5, 0) * mm, "radius": 25.4 * mm, "construction": true});
            skLineSegment(sketch, "E72.0", {"start": v(-88.9, 0) * mm, "end": v(-81.46, 17.96) * mm});
            skLineSegment(sketch, "E72.1", {"start": v(-81.46, 17.96) * mm, "end": v(-63.5, 25.4) * mm});
            skLineSegment(sketch, "E72.2", {"start": v(-63.5, 25.4) * mm, "end": v(-45.54, 17.96) * mm});
            skLineSegment(sketch, "E72.3", {"start": v(-45.54, 17.96) * mm, "end": v(-38.1, 0) * mm});
            skLineSegment(sketch, "E72.4", {"start": v(-38.1, 0) * mm, "end": v(-45.54, -17.96) * mm});
            skLineSegment(sketch, "E72.5", {"start": v(-45.54, -17.96) * mm, "end": v(-63.5, -25.4) * mm});
            skLineSegment(sketch, "E72.6", {"start": v(-63.5, -25.4) * mm, "end": v(-81.46, -17.96) * mm});
            skLineSegment(sketch, "E72.7", {"start": v(-81.46, -17.96) * mm, "end": v(-88.9, 0) * mm});
            skCircle(sketch, "E73.cCircle", {"center": v(-63.5, -63.5) * mm, "radius": 25.4 * mm, "construction": true});
            skLineSegment(sketch, "E73.0", {"start": v(-88.9, -63.5) * mm, "end": v(-81.46, -45.54) * mm});
            skLineSegment(sketch, "E73.1", {"start": v(-81.46, -45.54) * mm, "end": v(-63.5, -38.1) * mm});
            skLineSegment(sketch, "E73.2", {"start": v(-63.5, -38.1) * mm, "end": v(-45.54, -45.54) * mm});
            skLineSegment(sketch, "E73.3", {"start": v(-45.54, -45.54) * mm, "end": v(-38.1, -63.5) * mm});
            skLineSegment(sketch, "E73.4", {"start": v(-38.1, -63.5) * mm, "end": v(-45.54, -81.46) * mm});
            skLineSegment(sketch, "E73.5", {"start": v(-45.54, -81.46) * mm, "end": v(-63.5, -88.9) * mm});
            skLineSegment(sketch, "E73.6", {"start": v(-63.5, -88.9) * mm, "end": v(-81.46, -81.46) * mm});
            skLineSegment(sketch, "E73.7", {"start": v(-81.46, -81.46) * mm, "end": v(-88.9, -63.5) * mm});
            skCircle(sketch, "E74.cCircle", {"center": v(0, -63.5) * mm, "radius": 25.4 * mm, "construction": true});
            skLineSegment(sketch, "E74.0", {"start": v(-25.4, -63.5) * mm, "end": v(-17.96, -45.54) * mm});
            skLineSegment(sketch, "E74.1", {"start": v(-17.96, -45.54) * mm, "end": v(0, -38.1) * mm});
            skLineSegment(sketch, "E74.2", {"start": v(0, -38.1) * mm, "end": v(17.96, -45.54) * mm});
            skLineSegment(sketch, "E74.3", {"start": v(17.96, -45.54) * mm, "end": v(25.4, -63.5) * mm});
            skLineSegment(sketch, "E74.4", {"start": v(25.4, -63.5) * mm, "end": v(17.96, -81.46) * mm});
            skLineSegment(sketch, "E74.5", {"start": v(17.96, -81.46) * mm, "end": v(0, -88.9) * mm});
            skLineSegment(sketch, "E74.6", {"start": v(0, -88.9) * mm, "end": v(-17.96, -81.46) * mm});
            skLineSegment(sketch, "E74.7", {"start": v(-17.96, -81.46) * mm, "end": v(-25.4, -63.5) * mm});
            skCircle(sketch, "E75.cCircle", {"center": v(63.5, -63.5) * mm, "radius": 25.4 * mm, "construction": true});
            skLineSegment(sketch, "E75.0", {"start": v(38.1, -63.5) * mm, "end": v(45.54, -45.54) * mm});
            skLineSegment(sketch, "E75.1", {"start": v(45.54, -45.54) * mm, "end": v(63.5, -38.1) * mm});
            skLineSegment(sketch, "E75.2", {"start": v(63.5, -38.1) * mm, "end": v(81.46, -45.54) * mm});
            skLineSegment(sketch, "E75.3", {"start": v(81.46, -45.54) * mm, "end": v(88.9, -63.5) * mm});
            skLineSegment(sketch, "E75.4", {"start": v(88.9, -63.5) * mm, "end": v(81.46, -81.46) * mm});
            skLineSegment(sketch, "E75.5", {"start": v(81.46, -81.46) * mm, "end": v(63.5, -88.9) * mm});
            skLineSegment(sketch, "E75.6", {"start": v(63.5, -88.9) * mm, "end": v(45.54, -81.46) * mm});
            skLineSegment(sketch, "E75.7", {"start": v(45.54, -81.46) * mm, "end": v(38.1, -63.5) * mm});
            skSolve(sketch);
        }
        {
            var Q0;
            Q0=makeQuery(id+"F2.opExtrude","SWEPT_FACE",FACE,{"disambiguationData":[OSD([sQuery(id+"F1.wireOp",EDGE,"E25.right")])]});
            var sketch = newSketch(context, id + "F5", { "sketchPlane" : qUnion([Q0])});
            skLineSegment(sketch, "E76.bottom", {"start": v(254, -127) * mm, "end": v(0, -127) * mm});
            skLineSegment(sketch, "E76.top", {"start": v(254, 127) * mm, "end": v(0, 127) * mm});
            skLineSegment(sketch, "E76.left", {"start": v(254, -127) * mm, "end": v(254, 127) * mm});
            skLineSegment(sketch, "E76.right", {"start": v(0, -127) * mm, "end": v(0, 127) * mm});
            skPoint(sketch, "E76.middle", {"position": v(127, 0) * mm});
            skLineSegment(sketch, "E77", {"start": v(63.5, 127) * mm, "end": v(63.5, -127) * mm, "construction": true});
            skLineSegment(sketch, "E78", {"start": v(127, -127) * mm, "end": v(127, 127) * mm, "construction": true});
            skLineSegment(sketch, "E79", {"start": v(190.5, 127) * mm, "end": v(190.5, -127) * mm, "construction": true});
            skLineSegment(sketch, "E80", {"start": v(0, 63.5) * mm, "end": v(254, 63.5) * mm, "construction": true});
            skLineSegment(sketch, "E81", {"start": v(0, 0) * mm, "end": v(254, 0) * mm, "construction": true});
            skLineSegment(sketch, "E82", {"start": v(0, -63.5) * mm, "end": v(254, -63.5) * mm, "construction": true});
            skLineSegment(sketch, "E83.bottom", {"start": v(88.9, 38.1) * mm, "end": v(38.1, 38.1) * mm});
            skLineSegment(sketch, "E83.top", {"start": v(88.9, 88.9) * mm, "end": v(38.1, 88.9) * mm});
            skLineSegment(sketch, "E83.left", {"start": v(88.9, 38.1) * mm, "end": v(88.9, 88.9) * mm});
            skLineSegment(sketch, "E83.right", {"start": v(38.1, 38.1) * mm, "end": v(38.1, 88.9) * mm});
            skPoint(sketch, "E83.middle", {"position": v(63.5, 63.5) * mm});
            skLineSegment(sketch, "E84.bottom", {"start": v(152.4, 38.1) * mm, "end": v(101.6, 38.1) * mm});
            skLineSegment(sketch, "E84.top", {"start": v(152.4, 88.9) * mm, "end": v(101.6, 88.9) * mm});
            skLineSegment(sketch, "E84.left", {"start": v(152.4, 38.1) * mm, "end": v(152.4, 88.9) * mm});
            skLineSegment(sketch, "E84.right", {"start": v(101.6, 38.1) * mm, "end": v(101.6, 88.9) * mm});
            skPoint(sketch, "E84.middle", {"position": v(127, 63.5) * mm});
            skLineSegment(sketch, "E85.bottom", {"start": v(215.9, 38.1) * mm, "end": v(165.1, 38.1) * mm});
            skLineSegment(sketch, "E85.top", {"start": v(215.9, 88.9) * mm, "end": v(165.1, 88.9) * mm});
            skLineSegment(sketch, "E85.left", {"start": v(215.9, 38.1) * mm, "end": v(215.9, 88.9) * mm});
            skLineSegment(sketch, "E85.right", {"start": v(165.1, 38.1) * mm, "end": v(165.1, 88.9) * mm});
            skPoint(sketch, "E85.middle", {"position": v(190.5, 63.5) * mm});
            skLineSegment(sketch, "E86.bottom", {"start": v(88.9, -25.4) * mm, "end": v(38.1, -25.4) * mm});
            skLineSegment(sketch, "E86.top", {"start": v(88.9, 25.4) * mm, "end": v(38.1, 25.4) * mm});
            skLineSegment(sketch, "E86.left", {"start": v(88.9, -25.4) * mm, "end": v(88.9, 25.4) * mm});
            skLineSegment(sketch, "E86.right", {"start": v(38.1, -25.4) * mm, "end": v(38.1, 25.4) * mm});
            skPoint(sketch, "E86.middle", {"position": v(63.5, 0) * mm});
            skLineSegment(sketch, "E87.bottom", {"start": v(152.4, -25.4) * mm, "end": v(101.6, -25.4) * mm});
            skLineSegment(sketch, "E87.top", {"start": v(152.4, 25.4) * mm, "end": v(101.6, 25.4) * mm});
            skLineSegment(sketch, "E87.left", {"start": v(152.4, -25.4) * mm, "end": v(152.4, 25.4) * mm});
            skLineSegment(sketch, "E87.right", {"start": v(101.6, -25.4) * mm, "end": v(101.6, 25.4) * mm});
            skLineSegment(sketch, "E88.bottom", {"start": v(215.9, -25.4) * mm, "end": v(165.1, -25.4) * mm});
            skLineSegment(sketch, "E88.top", {"start": v(215.9, 25.4) * mm, "end": v(165.1, 25.4) * mm});
            skLineSegment(sketch, "E88.left", {"start": v(215.9, -25.4) * mm, "end": v(215.9, 25.4) * mm});
            skLineSegment(sketch, "E88.right", {"start": v(165.1, -25.4) * mm, "end": v(165.1, 25.4) * mm});
            skPoint(sketch, "E88.middle", {"position": v(190.5, 0) * mm});
            skLineSegment(sketch, "E89.bottom", {"start": v(88.9, -88.9) * mm, "end": v(38.1, -88.9) * mm});
            skLineSegment(sketch, "E89.top", {"start": v(88.9, -38.1) * mm, "end": v(38.1, -38.1) * mm});
            skLineSegment(sketch, "E89.left", {"start": v(88.9, -88.9) * mm, "end": v(88.9, -38.1) * mm});
            skLineSegment(sketch, "E89.right", {"start": v(38.1, -88.9) * mm, "end": v(38.1, -38.1) * mm});
            skPoint(sketch, "E89.middle", {"position": v(63.5, -63.5) * mm});
            skLineSegment(sketch, "E90.bottom", {"start": v(152.4, -88.9) * mm, "end": v(101.6, -88.9) * mm});
            skLineSegment(sketch, "E90.top", {"start": v(152.4, -38.1) * mm, "end": v(101.6, -38.1) * mm});
            skLineSegment(sketch, "E90.left", {"start": v(152.4, -88.9) * mm, "end": v(152.4, -38.1) * mm});
            skLineSegment(sketch, "E90.right", {"start": v(101.6, -88.9) * mm, "end": v(101.6, -38.1) * mm});
            skPoint(sketch, "E90.middle", {"position": v(127, -63.5) * mm});
            skLineSegment(sketch, "E91.bottom", {"start": v(215.9, -88.9) * mm, "end": v(165.1, -88.9) * mm});
            skLineSegment(sketch, "E91.top", {"start": v(215.9, -38.1) * mm, "end": v(165.1, -38.1) * mm});
            skLineSegment(sketch, "E91.left", {"start": v(215.9, -88.9) * mm, "end": v(215.9, -38.1) * mm});
            skLineSegment(sketch, "E91.right", {"start": v(165.1, -88.9) * mm, "end": v(165.1, -38.1) * mm});
            skPoint(sketch, "E91.middle", {"position": v(190.5, -63.5) * mm});
            skCircle(sketch, "E92.cCircle", {"center": v(63.5, 63.5) * mm, "radius": 25.4 * mm, "construction": true});
            skLineSegment(sketch, "E92.0", {"start": v(38.1, 63.5) * mm, "end": v(45.54, 81.46) * mm});
            skLineSegment(sketch, "E92.1", {"start": v(45.54, 81.46) * mm, "end": v(63.5, 88.9) * mm});
            skLineSegment(sketch, "E92.2", {"start": v(63.5, 88.9) * mm, "end": v(81.46, 81.46) * mm});
            skLineSegment(sketch, "E92.3", {"start": v(81.46, 81.46) * mm, "end": v(88.9, 63.5) * mm});
            skLineSegment(sketch, "E92.4", {"start": v(88.9, 63.5) * mm, "end": v(81.46, 45.54) * mm});
            skLineSegment(sketch, "E92.5", {"start": v(81.46, 45.54) * mm, "end": v(63.5, 38.1) * mm});
            skLineSegment(sketch, "E92.6", {"start": v(63.5, 38.1) * mm, "end": v(45.54, 45.54) * mm});
            skLineSegment(sketch, "E92.7", {"start": v(45.54, 45.54) * mm, "end": v(38.1, 63.5) * mm});
            skCircle(sketch, "E93.cCircle", {"center": v(127, 63.5) * mm, "radius": 25.4 * mm, "construction": true});
            skLineSegment(sketch, "E93.0", {"start": v(101.6, 63.5) * mm, "end": v(109.04, 81.46) * mm});
            skLineSegment(sketch, "E93.1", {"start": v(109.04, 81.46) * mm, "end": v(127, 88.9) * mm});
            skLineSegment(sketch, "E93.2", {"start": v(127, 88.9) * mm, "end": v(144.96, 81.46) * mm});
            skLineSegment(sketch, "E93.3", {"start": v(144.96, 81.46) * mm, "end": v(152.4, 63.5) * mm});
            skLineSegment(sketch, "E93.4", {"start": v(152.4, 63.5) * mm, "end": v(144.96, 45.54) * mm});
            skLineSegment(sketch, "E93.5", {"start": v(144.96, 45.54) * mm, "end": v(127, 38.1) * mm});
            skLineSegment(sketch, "E93.6", {"start": v(127, 38.1) * mm, "end": v(109.04, 45.54) * mm});
            skLineSegment(sketch, "E93.7", {"start": v(109.04, 45.54) * mm, "end": v(101.6, 63.5) * mm});
            skCircle(sketch, "E94.cCircle", {"center": v(190.5, 63.5) * mm, "radius": 25.4 * mm, "construction": true});
            skLineSegment(sketch, "E94.0", {"start": v(165.1, 63.5) * mm, "end": v(172.54, 81.46) * mm});
            skLineSegment(sketch, "E94.1", {"start": v(172.54, 81.46) * mm, "end": v(190.5, 88.9) * mm});
            skLineSegment(sketch, "E94.2", {"start": v(190.5, 88.9) * mm, "end": v(208.46, 81.46) * mm});
            skLineSegment(sketch, "E94.3", {"start": v(208.46, 81.46) * mm, "end": v(215.9, 63.5) * mm});
            skLineSegment(sketch, "E94.4", {"start": v(215.9, 63.5) * mm, "end": v(208.46, 45.54) * mm});
            skLineSegment(sketch, "E94.5", {"start": v(208.46, 45.54) * mm, "end": v(190.5, 38.1) * mm});
            skLineSegment(sketch, "E94.6", {"start": v(190.5, 38.1) * mm, "end": v(172.54, 45.54) * mm});
            skLineSegment(sketch, "E94.7", {"start": v(172.54, 45.54) * mm, "end": v(165.1, 63.5) * mm});
            skCircle(sketch, "E95.cCircle", {"center": v(190.5, 0) * mm, "radius": 25.4 * mm, "construction": true});
            skLineSegment(sketch, "E95.0", {"start": v(165.1, 0) * mm, "end": v(172.54, 17.96) * mm});
            skLineSegment(sketch, "E95.1", {"start": v(172.54, 17.96) * mm, "end": v(190.5, 25.4) * mm});
            skLineSegment(sketch, "E95.2", {"start": v(190.5, 25.4) * mm, "end": v(208.46, 17.96) * mm});
            skLineSegment(sketch, "E95.3", {"start": v(208.46, 17.96) * mm, "end": v(215.9, 0) * mm});
            skLineSegment(sketch, "E95.4", {"start": v(215.9, 0) * mm, "end": v(208.46, -17.96) * mm});
            skLineSegment(sketch, "E95.5", {"start": v(208.46, -17.96) * mm, "end": v(190.5, -25.4) * mm});
            skLineSegment(sketch, "E95.6", {"start": v(190.5, -25.4) * mm, "end": v(172.54, -17.96) * mm});
            skLineSegment(sketch, "E95.7", {"start": v(172.54, -17.96) * mm, "end": v(165.1, 0) * mm});
            skCircle(sketch, "E96.cCircle", {"center": v(127, 0) * mm, "radius": 25.4 * mm, "construction": true});
            skLineSegment(sketch, "E96.0", {"start": v(101.6, 0) * mm, "end": v(109.04, 17.96) * mm});
            skLineSegment(sketch, "E96.1", {"start": v(109.04, 17.96) * mm, "end": v(127, 25.4) * mm});
            skLineSegment(sketch, "E96.2", {"start": v(127, 25.4) * mm, "end": v(144.96, 17.96) * mm});
            skLineSegment(sketch, "E96.3", {"start": v(144.96, 17.96) * mm, "end": v(152.4, 0) * mm});
            skLineSegment(sketch, "E96.4", {"start": v(152.4, 0) * mm, "end": v(144.96, -17.96) * mm});
            skLineSegment(sketch, "E96.5", {"start": v(144.96, -17.96) * mm, "end": v(127, -25.4) * mm});
            skLineSegment(sketch, "E96.6", {"start": v(127, -25.4) * mm, "end": v(109.04, -17.96) * mm});
            skLineSegment(sketch, "E96.7", {"start": v(109.04, -17.96) * mm, "end": v(101.6, 0) * mm});
            skCircle(sketch, "E97.cCircle", {"center": v(63.5, 0) * mm, "radius": 25.4 * mm, "construction": true});
            skLineSegment(sketch, "E97.0", {"start": v(38.1, 0) * mm, "end": v(45.54, 17.96) * mm});
            skLineSegment(sketch, "E97.1", {"start": v(45.54, 17.96) * mm, "end": v(63.5, 25.4) * mm});
            skLineSegment(sketch, "E97.2", {"start": v(63.5, 25.4) * mm, "end": v(81.46, 17.96) * mm});
            skLineSegment(sketch, "E97.3", {"start": v(81.46, 17.96) * mm, "end": v(88.9, 0) * mm});
            skLineSegment(sketch, "E97.4", {"start": v(88.9, 0) * mm, "end": v(81.46, -17.96) * mm});
            skLineSegment(sketch, "E97.5", {"start": v(81.46, -17.96) * mm, "end": v(63.5, -25.4) * mm});
            skLineSegment(sketch, "E97.6", {"start": v(63.5, -25.4) * mm, "end": v(45.54, -17.96) * mm});
            skLineSegment(sketch, "E97.7", {"start": v(45.54, -17.96) * mm, "end": v(38.1, 0) * mm});
            skCircle(sketch, "E98.cCircle", {"center": v(63.5, -63.5) * mm, "radius": 25.4 * mm, "construction": true});
            skLineSegment(sketch, "E98.0", {"start": v(38.1, -63.5) * mm, "end": v(45.54, -45.54) * mm});
            skLineSegment(sketch, "E98.1", {"start": v(45.54, -45.54) * mm, "end": v(63.5, -38.1) * mm});
            skLineSegment(sketch, "E98.2", {"start": v(63.5, -38.1) * mm, "end": v(81.46, -45.54) * mm});
            skLineSegment(sketch, "E98.3", {"start": v(81.46, -45.54) * mm, "end": v(88.9, -63.5) * mm});
            skLineSegment(sketch, "E98.4", {"start": v(88.9, -63.5) * mm, "end": v(81.46, -81.46) * mm});
            skLineSegment(sketch, "E98.5", {"start": v(81.46, -81.46) * mm, "end": v(63.5, -88.9) * mm});
            skLineSegment(sketch, "E98.6", {"start": v(63.5, -88.9) * mm, "end": v(45.54, -81.46) * mm});
            skLineSegment(sketch, "E98.7", {"start": v(45.54, -81.46) * mm, "end": v(38.1, -63.5) * mm});
            skCircle(sketch, "E99.cCircle", {"center": v(127, -63.5) * mm, "radius": 25.4 * mm, "construction": true});
            skLineSegment(sketch, "E99.0", {"start": v(101.6, -63.5) * mm, "end": v(109.04, -45.54) * mm});
            skLineSegment(sketch, "E99.1", {"start": v(109.04, -45.54) * mm, "end": v(127, -38.1) * mm});
            skLineSegment(sketch, "E99.2", {"start": v(127, -38.1) * mm, "end": v(144.96, -45.54) * mm});
            skLineSegment(sketch, "E99.3", {"start": v(144.96, -45.54) * mm, "end": v(152.4, -63.5) * mm});
            skLineSegment(sketch, "E99.4", {"start": v(152.4, -63.5) * mm, "end": v(144.96, -81.46) * mm});
            skLineSegment(sketch, "E99.5", {"start": v(144.96, -81.46) * mm, "end": v(127, -88.9) * mm});
            skLineSegment(sketch, "E99.6", {"start": v(127, -88.9) * mm, "end": v(109.04, -81.46) * mm});
            skLineSegment(sketch, "E99.7", {"start": v(109.04, -81.46) * mm, "end": v(101.6, -63.5) * mm});
            skCircle(sketch, "E100.cCircle", {"center": v(190.5, -63.5) * mm, "radius": 25.4 * mm, "construction": true});
            skLineSegment(sketch, "E100.0", {"start": v(165.1, -63.5) * mm, "end": v(172.54, -45.54) * mm});
            skLineSegment(sketch, "E100.1", {"start": v(172.54, -45.54) * mm, "end": v(190.5, -38.1) * mm});
            skLineSegment(sketch, "E100.2", {"start": v(190.5, -38.1) * mm, "end": v(208.46, -45.54) * mm});
            skLineSegment(sketch, "E100.3", {"start": v(208.46, -45.54) * mm, "end": v(215.9, -63.5) * mm});
            skLineSegment(sketch, "E100.4", {"start": v(215.9, -63.5) * mm, "end": v(208.46, -81.46) * mm});
            skLineSegment(sketch, "E100.5", {"start": v(208.46, -81.46) * mm, "end": v(190.5, -88.9) * mm});
            skLineSegment(sketch, "E100.6", {"start": v(190.5, -88.9) * mm, "end": v(172.54, -81.46) * mm});
            skLineSegment(sketch, "E100.7", {"start": v(172.54, -81.46) * mm, "end": v(165.1, -63.5) * mm});
            skSolve(sketch);
        }
        {
            var Q0;
            Q0=makeQuery(id+"F2.opExtrude","SWEPT_FACE",FACE,{"disambiguationData":[OSD([sQuery(id+"F1.wireOp",EDGE,"E25.bottom")])]});
            var sketch = newSketch(context, id + "F6", { "sketchPlane" : qUnion([Q0])});
            skLineSegment(sketch, "E101.bottom", {"start": v(127, 0) * mm, "end": v(-127, 0) * mm});
            skLineSegment(sketch, "E101.top", {"start": v(127, 254) * mm, "end": v(-127, 254) * mm});
            skLineSegment(sketch, "E101.left", {"start": v(127, 0) * mm, "end": v(127, 254) * mm});
            skLineSegment(sketch, "E101.right", {"start": v(-127, 0) * mm, "end": v(-127, 254) * mm});
            skPoint(sketch, "E101.middle", {"position": v(0, 127) * mm});
            skLineSegment(sketch, "E102", {"start": v(-63.5, 254) * mm, "end": v(-63.5, 0) * mm, "construction": true});
            skLineSegment(sketch, "E103", {"start": v(0, 0) * mm, "end": v(0, 254) * mm, "construction": true});
            skLineSegment(sketch, "E104", {"start": v(63.5, 254) * mm, "end": v(63.5, 0) * mm, "construction": true});
            skLineSegment(sketch, "E105", {"start": v(-127, 190.5) * mm, "end": v(127, 190.5) * mm, "construction": true});
            skLineSegment(sketch, "E106", {"start": v(-127, 127) * mm, "end": v(127, 127) * mm, "construction": true});
            skLineSegment(sketch, "E107", {"start": v(-127, 63.5) * mm, "end": v(127, 63.5) * mm, "construction": true});
            skLineSegment(sketch, "E108.bottom", {"start": v(-38.1, 165.1) * mm, "end": v(-88.9, 165.1) * mm});
            skLineSegment(sketch, "E108.top", {"start": v(-38.1, 215.9) * mm, "end": v(-88.9, 215.9) * mm});
            skLineSegment(sketch, "E108.left", {"start": v(-38.1, 165.1) * mm, "end": v(-38.1, 215.9) * mm});
            skLineSegment(sketch, "E108.right", {"start": v(-88.9, 165.1) * mm, "end": v(-88.9, 215.9) * mm});
            skPoint(sketch, "E108.middle", {"position": v(-63.5, 190.5) * mm});
            skLineSegment(sketch, "E109.bottom", {"start": v(25.4, 165.1) * mm, "end": v(-25.4, 165.1) * mm});
            skLineSegment(sketch, "E109.top", {"start": v(25.4, 215.9) * mm, "end": v(-25.4, 215.9) * mm});
            skLineSegment(sketch, "E109.left", {"start": v(25.4, 165.1) * mm, "end": v(25.4, 215.9) * mm});
            skLineSegment(sketch, "E109.right", {"start": v(-25.4, 165.1) * mm, "end": v(-25.4, 215.9) * mm});
            skPoint(sketch, "E109.middle", {"position": v(0, 190.5) * mm});
            skLineSegment(sketch, "E110.bottom", {"start": v(88.9, 165.1) * mm, "end": v(38.1, 165.1) * mm});
            skLineSegment(sketch, "E110.top", {"start": v(88.9, 215.9) * mm, "end": v(38.1, 215.9) * mm});
            skLineSegment(sketch, "E110.left", {"start": v(88.9, 165.1) * mm, "end": v(88.9, 215.9) * mm});
            skLineSegment(sketch, "E110.right", {"start": v(38.1, 165.1) * mm, "end": v(38.1, 215.9) * mm});
            skPoint(sketch, "E110.middle", {"position": v(63.5, 190.5) * mm});
            skLineSegment(sketch, "E111.bottom", {"start": v(-38.1, 101.6) * mm, "end": v(-88.9, 101.6) * mm});
            skLineSegment(sketch, "E111.top", {"start": v(-38.1, 152.4) * mm, "end": v(-88.9, 152.4) * mm});
            skLineSegment(sketch, "E111.left", {"start": v(-38.1, 101.6) * mm, "end": v(-38.1, 152.4) * mm});
            skLineSegment(sketch, "E111.right", {"start": v(-88.9, 101.6) * mm, "end": v(-88.9, 152.4) * mm});
            skPoint(sketch, "E111.middle", {"position": v(-63.5, 127) * mm});
            skLineSegment(sketch, "E112.bottom", {"start": v(25.4, 101.6) * mm, "end": v(-25.4, 101.6) * mm});
            skLineSegment(sketch, "E112.top", {"start": v(25.4, 152.4) * mm, "end": v(-25.4, 152.4) * mm});
            skLineSegment(sketch, "E112.left", {"start": v(25.4, 101.6) * mm, "end": v(25.4, 152.4) * mm});
            skLineSegment(sketch, "E112.right", {"start": v(-25.4, 101.6) * mm, "end": v(-25.4, 152.4) * mm});
            skLineSegment(sketch, "E113.bottom", {"start": v(88.9, 101.6) * mm, "end": v(38.1, 101.6) * mm});
            skLineSegment(sketch, "E113.top", {"start": v(88.9, 152.4) * mm, "end": v(38.1, 152.4) * mm});
            skLineSegment(sketch, "E113.left", {"start": v(88.9, 101.6) * mm, "end": v(88.9, 152.4) * mm});
            skLineSegment(sketch, "E113.right", {"start": v(38.1, 101.6) * mm, "end": v(38.1, 152.4) * mm});
            skPoint(sketch, "E113.middle", {"position": v(63.5, 127) * mm});
            skLineSegment(sketch, "E114.bottom", {"start": v(-38.1, 38.1) * mm, "end": v(-88.9, 38.1) * mm});
            skLineSegment(sketch, "E114.top", {"start": v(-38.1, 88.9) * mm, "end": v(-88.9, 88.9) * mm});
            skLineSegment(sketch, "E114.left", {"start": v(-38.1, 38.1) * mm, "end": v(-38.1, 88.9) * mm});
            skLineSegment(sketch, "E114.right", {"start": v(-88.9, 38.1) * mm, "end": v(-88.9, 88.9) * mm});
            skPoint(sketch, "E114.middle", {"position": v(-63.5, 63.5) * mm});
            skLineSegment(sketch, "E115.bottom", {"start": v(25.4, 38.1) * mm, "end": v(-25.4, 38.1) * mm});
            skLineSegment(sketch, "E115.top", {"start": v(25.4, 88.9) * mm, "end": v(-25.4, 88.9) * mm});
            skLineSegment(sketch, "E115.left", {"start": v(25.4, 38.1) * mm, "end": v(25.4, 88.9) * mm});
            skLineSegment(sketch, "E115.right", {"start": v(-25.4, 38.1) * mm, "end": v(-25.4, 88.9) * mm});
            skPoint(sketch, "E115.middle", {"position": v(0, 63.5) * mm});
            skLineSegment(sketch, "E116.bottom", {"start": v(88.9, 38.1) * mm, "end": v(38.1, 38.1) * mm});
            skLineSegment(sketch, "E116.top", {"start": v(88.9, 88.9) * mm, "end": v(38.1, 88.9) * mm});
            skLineSegment(sketch, "E116.left", {"start": v(88.9, 38.1) * mm, "end": v(88.9, 88.9) * mm});
            skLineSegment(sketch, "E116.right", {"start": v(38.1, 38.1) * mm, "end": v(38.1, 88.9) * mm});
            skPoint(sketch, "E116.middle", {"position": v(63.5, 63.5) * mm});
            skCircle(sketch, "E117.cCircle", {"center": v(-63.5, 190.5) * mm, "radius": 25.4 * mm, "construction": true});
            skLineSegment(sketch, "E117.0", {"start": v(-88.9, 190.5) * mm, "end": v(-81.46, 208.46) * mm});
            skLineSegment(sketch, "E117.1", {"start": v(-81.46, 208.46) * mm, "end": v(-63.5, 215.9) * mm});
            skLineSegment(sketch, "E117.2", {"start": v(-63.5, 215.9) * mm, "end": v(-45.54, 208.46) * mm});
            skLineSegment(sketch, "E117.3", {"start": v(-45.54, 208.46) * mm, "end": v(-38.1, 190.5) * mm});
            skLineSegment(sketch, "E117.4", {"start": v(-38.1, 190.5) * mm, "end": v(-45.54, 172.54) * mm});
            skLineSegment(sketch, "E117.5", {"start": v(-45.54, 172.54) * mm, "end": v(-63.5, 165.1) * mm});
            skLineSegment(sketch, "E117.6", {"start": v(-63.5, 165.1) * mm, "end": v(-81.46, 172.54) * mm});
            skLineSegment(sketch, "E117.7", {"start": v(-81.46, 172.54) * mm, "end": v(-88.9, 190.5) * mm});
            skCircle(sketch, "E118.cCircle", {"center": v(0, 190.5) * mm, "radius": 25.4 * mm, "construction": true});
            skLineSegment(sketch, "E118.0", {"start": v(-25.4, 190.5) * mm, "end": v(-17.96, 208.46) * mm});
            skLineSegment(sketch, "E118.1", {"start": v(-17.96, 208.46) * mm, "end": v(0, 215.9) * mm});
            skLineSegment(sketch, "E118.2", {"start": v(0, 215.9) * mm, "end": v(17.96, 208.46) * mm});
            skLineSegment(sketch, "E118.3", {"start": v(17.96, 208.46) * mm, "end": v(25.4, 190.5) * mm});
            skLineSegment(sketch, "E118.4", {"start": v(25.4, 190.5) * mm, "end": v(17.96, 172.54) * mm});
            skLineSegment(sketch, "E118.5", {"start": v(17.96, 172.54) * mm, "end": v(0, 165.1) * mm});
            skLineSegment(sketch, "E118.6", {"start": v(0, 165.1) * mm, "end": v(-17.96, 172.54) * mm});
            skLineSegment(sketch, "E118.7", {"start": v(-17.96, 172.54) * mm, "end": v(-25.4, 190.5) * mm});
            skCircle(sketch, "E119.cCircle", {"center": v(63.5, 190.5) * mm, "radius": 25.4 * mm, "construction": true});
            skLineSegment(sketch, "E119.0", {"start": v(38.1, 190.5) * mm, "end": v(45.54, 208.46) * mm});
            skLineSegment(sketch, "E119.1", {"start": v(45.54, 208.46) * mm, "end": v(63.5, 215.9) * mm});
            skLineSegment(sketch, "E119.2", {"start": v(63.5, 215.9) * mm, "end": v(81.46, 208.46) * mm});
            skLineSegment(sketch, "E119.3", {"start": v(81.46, 208.46) * mm, "end": v(88.9, 190.5) * mm});
            skLineSegment(sketch, "E119.4", {"start": v(88.9, 190.5) * mm, "end": v(81.46, 172.54) * mm});
            skLineSegment(sketch, "E119.5", {"start": v(81.46, 172.54) * mm, "end": v(63.5, 165.1) * mm});
            skLineSegment(sketch, "E119.6", {"start": v(63.5, 165.1) * mm, "end": v(45.54, 172.54) * mm});
            skLineSegment(sketch, "E119.7", {"start": v(45.54, 172.54) * mm, "end": v(38.1, 190.5) * mm});
            skCircle(sketch, "E120.cCircle", {"center": v(63.5, 127) * mm, "radius": 25.4 * mm, "construction": true});
            skLineSegment(sketch, "E120.0", {"start": v(38.1, 127) * mm, "end": v(45.54, 144.96) * mm});
            skLineSegment(sketch, "E120.1", {"start": v(45.54, 144.96) * mm, "end": v(63.5, 152.4) * mm});
            skLineSegment(sketch, "E120.2", {"start": v(63.5, 152.4) * mm, "end": v(81.46, 144.96) * mm});
            skLineSegment(sketch, "E120.3", {"start": v(81.46, 144.96) * mm, "end": v(88.9, 127) * mm});
            skLineSegment(sketch, "E120.4", {"start": v(88.9, 127) * mm, "end": v(81.46, 109.04) * mm});
            skLineSegment(sketch, "E120.5", {"start": v(81.46, 109.04) * mm, "end": v(63.5, 101.6) * mm});
            skLineSegment(sketch, "E120.6", {"start": v(63.5, 101.6) * mm, "end": v(45.54, 109.04) * mm});
            skLineSegment(sketch, "E120.7", {"start": v(45.54, 109.04) * mm, "end": v(38.1, 127) * mm});
            skCircle(sketch, "E121.cCircle", {"center": v(0, 127) * mm, "radius": 25.4 * mm, "construction": true});
            skLineSegment(sketch, "E121.0", {"start": v(-25.4, 127) * mm, "end": v(-17.96, 144.96) * mm});
            skLineSegment(sketch, "E121.1", {"start": v(-17.96, 144.96) * mm, "end": v(0, 152.4) * mm});
            skLineSegment(sketch, "E121.2", {"start": v(0, 152.4) * mm, "end": v(17.96, 144.96) * mm});
            skLineSegment(sketch, "E121.3", {"start": v(17.96, 144.96) * mm, "end": v(25.4, 127) * mm});
            skLineSegment(sketch, "E121.4", {"start": v(25.4, 127) * mm, "end": v(17.96, 109.04) * mm});
            skLineSegment(sketch, "E121.5", {"start": v(17.96, 109.04) * mm, "end": v(0, 101.6) * mm});
            skLineSegment(sketch, "E121.6", {"start": v(0, 101.6) * mm, "end": v(-17.96, 109.04) * mm});
            skLineSegment(sketch, "E121.7", {"start": v(-17.96, 109.04) * mm, "end": v(-25.4, 127) * mm});
            skCircle(sketch, "E122.cCircle", {"center": v(-63.5, 127) * mm, "radius": 25.4 * mm, "construction": true});
            skLineSegment(sketch, "E122.0", {"start": v(-88.9, 127) * mm, "end": v(-81.46, 144.96) * mm});
            skLineSegment(sketch, "E122.1", {"start": v(-81.46, 144.96) * mm, "end": v(-63.5, 152.4) * mm});
            skLineSegment(sketch, "E122.2", {"start": v(-63.5, 152.4) * mm, "end": v(-45.54, 144.96) * mm});
            skLineSegment(sketch, "E122.3", {"start": v(-45.54, 144.96) * mm, "end": v(-38.1, 127) * mm});
            skLineSegment(sketch, "E122.4", {"start": v(-38.1, 127) * mm, "end": v(-45.54, 109.04) * mm});
            skLineSegment(sketch, "E122.5", {"start": v(-45.54, 109.04) * mm, "end": v(-63.5, 101.6) * mm});
            skLineSegment(sketch, "E122.6", {"start": v(-63.5, 101.6) * mm, "end": v(-81.46, 109.04) * mm});
            skLineSegment(sketch, "E122.7", {"start": v(-81.46, 109.04) * mm, "end": v(-88.9, 127) * mm});
            skCircle(sketch, "E123.cCircle", {"center": v(-63.5, 63.5) * mm, "radius": 25.4 * mm, "construction": true});
            skLineSegment(sketch, "E123.0", {"start": v(-88.9, 63.5) * mm, "end": v(-81.46, 81.46) * mm});
            skLineSegment(sketch, "E123.1", {"start": v(-81.46, 81.46) * mm, "end": v(-63.5, 88.9) * mm});
            skLineSegment(sketch, "E123.2", {"start": v(-63.5, 88.9) * mm, "end": v(-45.54, 81.46) * mm});
            skLineSegment(sketch, "E123.3", {"start": v(-45.54, 81.46) * mm, "end": v(-38.1, 63.5) * mm});
            skLineSegment(sketch, "E123.4", {"start": v(-38.1, 63.5) * mm, "end": v(-45.54, 45.54) * mm});
            skLineSegment(sketch, "E123.5", {"start": v(-45.54, 45.54) * mm, "end": v(-63.5, 38.1) * mm});
            skLineSegment(sketch, "E123.6", {"start": v(-63.5, 38.1) * mm, "end": v(-81.46, 45.54) * mm});
            skLineSegment(sketch, "E123.7", {"start": v(-81.46, 45.54) * mm, "end": v(-88.9, 63.5) * mm});
            skCircle(sketch, "E124.cCircle", {"center": v(0, 63.5) * mm, "radius": 25.4 * mm, "construction": true});
            skLineSegment(sketch, "E124.0", {"start": v(-25.4, 63.5) * mm, "end": v(-17.96, 81.46) * mm});
            skLineSegment(sketch, "E124.1", {"start": v(-17.96, 81.46) * mm, "end": v(0, 88.9) * mm});
            skLineSegment(sketch, "E124.2", {"start": v(0, 88.9) * mm, "end": v(17.96, 81.46) * mm});
            skLineSegment(sketch, "E124.3", {"start": v(17.96, 81.46) * mm, "end": v(25.4, 63.5) * mm});
            skLineSegment(sketch, "E124.4", {"start": v(25.4, 63.5) * mm, "end": v(17.96, 45.54) * mm});
            skLineSegment(sketch, "E124.5", {"start": v(17.96, 45.54) * mm, "end": v(0, 38.1) * mm});
            skLineSegment(sketch, "E124.6", {"start": v(0, 38.1) * mm, "end": v(-17.96, 45.54) * mm});
            skLineSegment(sketch, "E124.7", {"start": v(-17.96, 45.54) * mm, "end": v(-25.4, 63.5) * mm});
            skCircle(sketch, "E125.cCircle", {"center": v(63.5, 63.5) * mm, "radius": 25.4 * mm, "construction": true});
            skLineSegment(sketch, "E125.0", {"start": v(38.1, 63.5) * mm, "end": v(45.54, 81.46) * mm});
            skLineSegment(sketch, "E125.1", {"start": v(45.54, 81.46) * mm, "end": v(63.5, 88.9) * mm});
            skLineSegment(sketch, "E125.2", {"start": v(63.5, 88.9) * mm, "end": v(81.46, 81.46) * mm});
            skLineSegment(sketch, "E125.3", {"start": v(81.46, 81.46) * mm, "end": v(88.9, 63.5) * mm});
            skLineSegment(sketch, "E125.4", {"start": v(88.9, 63.5) * mm, "end": v(81.46, 45.54) * mm});
            skLineSegment(sketch, "E125.5", {"start": v(81.46, 45.54) * mm, "end": v(63.5, 38.1) * mm});
            skLineSegment(sketch, "E125.6", {"start": v(63.5, 38.1) * mm, "end": v(45.54, 45.54) * mm});
            skLineSegment(sketch, "E125.7", {"start": v(45.54, 45.54) * mm, "end": v(38.1, 63.5) * mm});
            skSolve(sketch);
        }
        {
            var Q0;
            Q0=makeQuery(id+"F2.opExtrude","SWEPT_FACE",FACE,{"disambiguationData":[OSD([sQuery(id+"F1.wireOp",EDGE,"E25.top")])]});
            var sketch = newSketch(context, id + "F7", { "sketchPlane" : qUnion([Q0])});
            skLineSegment(sketch, "E126.bottom", {"start": v(127, -254) * mm, "end": v(-127, -254) * mm});
            skLineSegment(sketch, "E126.top", {"start": v(127, 0) * mm, "end": v(-127, 0) * mm});
            skLineSegment(sketch, "E126.left", {"start": v(127, -254) * mm, "end": v(127, 0) * mm});
            skLineSegment(sketch, "E126.right", {"start": v(-127, -254) * mm, "end": v(-127, 0) * mm});
            skPoint(sketch, "E126.middle", {"position": v(0, -127) * mm});
            skLineSegment(sketch, "E127", {"start": v(-63.5, 0) * mm, "end": v(-63.5, -254) * mm, "construction": true});
            skLineSegment(sketch, "E128", {"start": v(0, -254) * mm, "end": v(0, 0) * mm, "construction": true});
            skLineSegment(sketch, "E129", {"start": v(63.5, 0) * mm, "end": v(63.5, -254) * mm, "construction": true});
            skLineSegment(sketch, "E130", {"start": v(-127, -63.5) * mm, "end": v(127, -63.5) * mm, "construction": true});
            skLineSegment(sketch, "E131", {"start": v(-127, -127) * mm, "end": v(127, -127) * mm, "construction": true});
            skLineSegment(sketch, "E132", {"start": v(-127, -190.5) * mm, "end": v(127, -190.5) * mm, "construction": true});
            skLineSegment(sketch, "E133.bottom", {"start": v(-38.1, -88.9) * mm, "end": v(-88.9, -88.9) * mm});
            skLineSegment(sketch, "E133.top", {"start": v(-38.1, -38.1) * mm, "end": v(-88.9, -38.1) * mm});
            skLineSegment(sketch, "E133.left", {"start": v(-38.1, -88.9) * mm, "end": v(-38.1, -38.1) * mm});
            skLineSegment(sketch, "E133.right", {"start": v(-88.9, -88.9) * mm, "end": v(-88.9, -38.1) * mm});
            skPoint(sketch, "E133.middle", {"position": v(-63.5, -63.5) * mm});
            skLineSegment(sketch, "E134.bottom", {"start": v(25.4, -88.9) * mm, "end": v(-25.4, -88.9) * mm});
            skLineSegment(sketch, "E134.top", {"start": v(25.4, -38.1) * mm, "end": v(-25.4, -38.1) * mm});
            skLineSegment(sketch, "E134.left", {"start": v(25.4, -88.9) * mm, "end": v(25.4, -38.1) * mm});
            skLineSegment(sketch, "E134.right", {"start": v(-25.4, -88.9) * mm, "end": v(-25.4, -38.1) * mm});
            skPoint(sketch, "E134.middle", {"position": v(0, -63.5) * mm});
            skLineSegment(sketch, "E135.bottom", {"start": v(88.9, -88.9) * mm, "end": v(38.1, -88.9) * mm});
            skLineSegment(sketch, "E135.top", {"start": v(88.9, -38.1) * mm, "end": v(38.1, -38.1) * mm});
            skLineSegment(sketch, "E135.left", {"start": v(88.9, -88.9) * mm, "end": v(88.9, -38.1) * mm});
            skLineSegment(sketch, "E135.right", {"start": v(38.1, -88.9) * mm, "end": v(38.1, -38.1) * mm});
            skPoint(sketch, "E135.middle", {"position": v(63.5, -63.5) * mm});
            skLineSegment(sketch, "E136.bottom", {"start": v(-38.1, -152.4) * mm, "end": v(-88.9, -152.4) * mm});
            skLineSegment(sketch, "E136.top", {"start": v(-38.1, -101.6) * mm, "end": v(-88.9, -101.6) * mm});
            skLineSegment(sketch, "E136.left", {"start": v(-38.1, -152.4) * mm, "end": v(-38.1, -101.6) * mm});
            skLineSegment(sketch, "E136.right", {"start": v(-88.9, -152.4) * mm, "end": v(-88.9, -101.6) * mm});
            skPoint(sketch, "E136.middle", {"position": v(-63.5, -127) * mm});
            skLineSegment(sketch, "E137.bottom", {"start": v(25.4, -152.4) * mm, "end": v(-25.4, -152.4) * mm});
            skLineSegment(sketch, "E137.top", {"start": v(25.4, -101.6) * mm, "end": v(-25.4, -101.6) * mm});
            skLineSegment(sketch, "E137.left", {"start": v(25.4, -152.4) * mm, "end": v(25.4, -101.6) * mm});
            skLineSegment(sketch, "E137.right", {"start": v(-25.4, -152.4) * mm, "end": v(-25.4, -101.6) * mm});
            skLineSegment(sketch, "E138.bottom", {"start": v(88.9, -152.4) * mm, "end": v(38.1, -152.4) * mm});
            skLineSegment(sketch, "E138.top", {"start": v(88.9, -101.6) * mm, "end": v(38.1, -101.6) * mm});
            skLineSegment(sketch, "E138.left", {"start": v(88.9, -152.4) * mm, "end": v(88.9, -101.6) * mm});
            skLineSegment(sketch, "E138.right", {"start": v(38.1, -152.4) * mm, "end": v(38.1, -101.6) * mm});
            skPoint(sketch, "E138.middle", {"position": v(63.5, -127) * mm});
            skLineSegment(sketch, "E139.bottom", {"start": v(-38.1, -215.9) * mm, "end": v(-88.9, -215.9) * mm});
            skLineSegment(sketch, "E139.top", {"start": v(-38.1, -165.1) * mm, "end": v(-88.9, -165.1) * mm});
            skLineSegment(sketch, "E139.left", {"start": v(-38.1, -215.9) * mm, "end": v(-38.1, -165.1) * mm});
            skLineSegment(sketch, "E139.right", {"start": v(-88.9, -215.9) * mm, "end": v(-88.9, -165.1) * mm});
            skPoint(sketch, "E139.middle", {"position": v(-63.5, -190.5) * mm});
            skLineSegment(sketch, "E140.bottom", {"start": v(25.4, -215.9) * mm, "end": v(-25.4, -215.9) * mm});
            skLineSegment(sketch, "E140.top", {"start": v(25.4, -165.1) * mm, "end": v(-25.4, -165.1) * mm});
            skLineSegment(sketch, "E140.left", {"start": v(25.4, -215.9) * mm, "end": v(25.4, -165.1) * mm});
            skLineSegment(sketch, "E140.right", {"start": v(-25.4, -215.9) * mm, "end": v(-25.4, -165.1) * mm});
            skPoint(sketch, "E140.middle", {"position": v(0, -190.5) * mm});
            skLineSegment(sketch, "E141.bottom", {"start": v(88.9, -215.9) * mm, "end": v(38.1, -215.9) * mm});
            skLineSegment(sketch, "E141.top", {"start": v(88.9, -165.1) * mm, "end": v(38.1, -165.1) * mm});
            skLineSegment(sketch, "E141.left", {"start": v(88.9, -215.9) * mm, "end": v(88.9, -165.1) * mm});
            skLineSegment(sketch, "E141.right", {"start": v(38.1, -215.9) * mm, "end": v(38.1, -165.1) * mm});
            skPoint(sketch, "E141.middle", {"position": v(63.5, -190.5) * mm});
            skCircle(sketch, "E142.cCircle", {"center": v(-63.5, -63.5) * mm, "radius": 25.4 * mm, "construction": true});
            skLineSegment(sketch, "E142.0", {"start": v(-88.9, -63.5) * mm, "end": v(-81.46, -45.54) * mm});
            skLineSegment(sketch, "E142.1", {"start": v(-81.46, -45.54) * mm, "end": v(-63.5, -38.1) * mm});
            skLineSegment(sketch, "E142.2", {"start": v(-63.5, -38.1) * mm, "end": v(-45.54, -45.54) * mm});
            skLineSegment(sketch, "E142.3", {"start": v(-45.54, -45.54) * mm, "end": v(-38.1, -63.5) * mm});
            skLineSegment(sketch, "E142.4", {"start": v(-38.1, -63.5) * mm, "end": v(-45.54, -81.46) * mm});
            skLineSegment(sketch, "E142.5", {"start": v(-45.54, -81.46) * mm, "end": v(-63.5, -88.9) * mm});
            skLineSegment(sketch, "E142.6", {"start": v(-63.5, -88.9) * mm, "end": v(-81.46, -81.46) * mm});
            skLineSegment(sketch, "E142.7", {"start": v(-81.46, -81.46) * mm, "end": v(-88.9, -63.5) * mm});
            skCircle(sketch, "E143.cCircle", {"center": v(0, -63.5) * mm, "radius": 25.4 * mm, "construction": true});
            skLineSegment(sketch, "E143.0", {"start": v(-25.4, -63.5) * mm, "end": v(-17.96, -45.54) * mm});
            skLineSegment(sketch, "E143.1", {"start": v(-17.96, -45.54) * mm, "end": v(0, -38.1) * mm});
            skLineSegment(sketch, "E143.2", {"start": v(0, -38.1) * mm, "end": v(17.96, -45.54) * mm});
            skLineSegment(sketch, "E143.3", {"start": v(17.96, -45.54) * mm, "end": v(25.4, -63.5) * mm});
            skLineSegment(sketch, "E143.4", {"start": v(25.4, -63.5) * mm, "end": v(17.96, -81.46) * mm});
            skLineSegment(sketch, "E143.5", {"start": v(17.96, -81.46) * mm, "end": v(0, -88.9) * mm});
            skLineSegment(sketch, "E143.6", {"start": v(0, -88.9) * mm, "end": v(-17.96, -81.46) * mm});
            skLineSegment(sketch, "E143.7", {"start": v(-17.96, -81.46) * mm, "end": v(-25.4, -63.5) * mm});
            skCircle(sketch, "E144.cCircle", {"center": v(63.5, -63.5) * mm, "radius": 25.4 * mm, "construction": true});
            skLineSegment(sketch, "E144.0", {"start": v(38.1, -63.5) * mm, "end": v(45.54, -45.54) * mm});
            skLineSegment(sketch, "E144.1", {"start": v(45.54, -45.54) * mm, "end": v(63.5, -38.1) * mm});
            skLineSegment(sketch, "E144.2", {"start": v(63.5, -38.1) * mm, "end": v(81.46, -45.54) * mm});
            skLineSegment(sketch, "E144.3", {"start": v(81.46, -45.54) * mm, "end": v(88.9, -63.5) * mm});
            skLineSegment(sketch, "E144.4", {"start": v(88.9, -63.5) * mm, "end": v(81.46, -81.46) * mm});
            skLineSegment(sketch, "E144.5", {"start": v(81.46, -81.46) * mm, "end": v(63.5, -88.9) * mm});
            skLineSegment(sketch, "E144.6", {"start": v(63.5, -88.9) * mm, "end": v(45.54, -81.46) * mm});
            skLineSegment(sketch, "E144.7", {"start": v(45.54, -81.46) * mm, "end": v(38.1, -63.5) * mm});
            skCircle(sketch, "E145.cCircle", {"center": v(63.5, -127) * mm, "radius": 25.4 * mm, "construction": true});
            skLineSegment(sketch, "E145.0", {"start": v(38.1, -127) * mm, "end": v(45.54, -109.04) * mm});
            skLineSegment(sketch, "E145.1", {"start": v(45.54, -109.04) * mm, "end": v(63.5, -101.6) * mm});
            skLineSegment(sketch, "E145.2", {"start": v(63.5, -101.6) * mm, "end": v(81.46, -109.04) * mm});
            skLineSegment(sketch, "E145.3", {"start": v(81.46, -109.04) * mm, "end": v(88.9, -127) * mm});
            skLineSegment(sketch, "E145.4", {"start": v(88.9, -127) * mm, "end": v(81.46, -144.96) * mm});
            skLineSegment(sketch, "E145.5", {"start": v(81.46, -144.96) * mm, "end": v(63.5, -152.4) * mm});
            skLineSegment(sketch, "E145.6", {"start": v(63.5, -152.4) * mm, "end": v(45.54, -144.96) * mm});
            skLineSegment(sketch, "E145.7", {"start": v(45.54, -144.96) * mm, "end": v(38.1, -127) * mm});
            skCircle(sketch, "E146.cCircle", {"center": v(0, -127) * mm, "radius": 25.4 * mm, "construction": true});
            skLineSegment(sketch, "E146.0", {"start": v(-25.4, -127) * mm, "end": v(-17.96, -109.04) * mm});
            skLineSegment(sketch, "E146.1", {"start": v(-17.96, -109.04) * mm, "end": v(0, -101.6) * mm});
            skLineSegment(sketch, "E146.2", {"start": v(0, -101.6) * mm, "end": v(17.96, -109.04) * mm});
            skLineSegment(sketch, "E146.3", {"start": v(17.96, -109.04) * mm, "end": v(25.4, -127) * mm});
            skLineSegment(sketch, "E146.4", {"start": v(25.4, -127) * mm, "end": v(17.96, -144.96) * mm});
            skLineSegment(sketch, "E146.5", {"start": v(17.96, -144.96) * mm, "end": v(0, -152.4) * mm});
            skLineSegment(sketch, "E146.6", {"start": v(0, -152.4) * mm, "end": v(-17.96, -144.96) * mm});
            skLineSegment(sketch, "E146.7", {"start": v(-17.96, -144.96) * mm, "end": v(-25.4, -127) * mm});
            skCircle(sketch, "E147.cCircle", {"center": v(-63.5, -127) * mm, "radius": 25.4 * mm, "construction": true});
            skLineSegment(sketch, "E147.0", {"start": v(-88.9, -127) * mm, "end": v(-81.46, -109.04) * mm});
            skLineSegment(sketch, "E147.1", {"start": v(-81.46, -109.04) * mm, "end": v(-63.5, -101.6) * mm});
            skLineSegment(sketch, "E147.2", {"start": v(-63.5, -101.6) * mm, "end": v(-45.54, -109.04) * mm});
            skLineSegment(sketch, "E147.3", {"start": v(-45.54, -109.04) * mm, "end": v(-38.1, -127) * mm});
            skLineSegment(sketch, "E147.4", {"start": v(-38.1, -127) * mm, "end": v(-45.54, -144.96) * mm});
            skLineSegment(sketch, "E147.5", {"start": v(-45.54, -144.96) * mm, "end": v(-63.5, -152.4) * mm});
            skLineSegment(sketch, "E147.6", {"start": v(-63.5, -152.4) * mm, "end": v(-81.46, -144.96) * mm});
            skLineSegment(sketch, "E147.7", {"start": v(-81.46, -144.96) * mm, "end": v(-88.9, -127) * mm});
            skCircle(sketch, "E148.cCircle", {"center": v(-63.5, -190.5) * mm, "radius": 25.4 * mm, "construction": true});
            skLineSegment(sketch, "E148.0", {"start": v(-88.9, -190.5) * mm, "end": v(-81.46, -172.54) * mm});
            skLineSegment(sketch, "E148.1", {"start": v(-81.46, -172.54) * mm, "end": v(-63.5, -165.1) * mm});
            skLineSegment(sketch, "E148.2", {"start": v(-63.5, -165.1) * mm, "end": v(-45.54, -172.54) * mm});
            skLineSegment(sketch, "E148.3", {"start": v(-45.54, -172.54) * mm, "end": v(-38.1, -190.5) * mm});
            skLineSegment(sketch, "E148.4", {"start": v(-38.1, -190.5) * mm, "end": v(-45.54, -208.46) * mm});
            skLineSegment(sketch, "E148.5", {"start": v(-45.54, -208.46) * mm, "end": v(-63.5, -215.9) * mm});
            skLineSegment(sketch, "E148.6", {"start": v(-63.5, -215.9) * mm, "end": v(-81.46, -208.46) * mm});
            skLineSegment(sketch, "E148.7", {"start": v(-81.46, -208.46) * mm, "end": v(-88.9, -190.5) * mm});
            skCircle(sketch, "E149.cCircle", {"center": v(0, -190.5) * mm, "radius": 25.4 * mm, "construction": true});
            skLineSegment(sketch, "E149.0", {"start": v(-25.4, -190.5) * mm, "end": v(-17.96, -172.54) * mm});
            skLineSegment(sketch, "E149.1", {"start": v(-17.96, -172.54) * mm, "end": v(0, -165.1) * mm});
            skLineSegment(sketch, "E149.2", {"start": v(0, -165.1) * mm, "end": v(17.96, -172.54) * mm});
            skLineSegment(sketch, "E149.3", {"start": v(17.96, -172.54) * mm, "end": v(25.4, -190.5) * mm});
            skLineSegment(sketch, "E149.4", {"start": v(25.4, -190.5) * mm, "end": v(17.96, -208.46) * mm});
            skLineSegment(sketch, "E149.5", {"start": v(17.96, -208.46) * mm, "end": v(0, -215.9) * mm});
            skLineSegment(sketch, "E149.6", {"start": v(0, -215.9) * mm, "end": v(-17.96, -208.46) * mm});
            skLineSegment(sketch, "E149.7", {"start": v(-17.96, -208.46) * mm, "end": v(-25.4, -190.5) * mm});
            skCircle(sketch, "E150.cCircle", {"center": v(63.5, -190.5) * mm, "radius": 25.4 * mm, "construction": true});
            skLineSegment(sketch, "E150.0", {"start": v(38.1, -190.5) * mm, "end": v(45.54, -172.54) * mm});
            skLineSegment(sketch, "E150.1", {"start": v(45.54, -172.54) * mm, "end": v(63.5, -165.1) * mm});
            skLineSegment(sketch, "E150.2", {"start": v(63.5, -165.1) * mm, "end": v(81.46, -172.54) * mm});
            skLineSegment(sketch, "E150.3", {"start": v(81.46, -172.54) * mm, "end": v(88.9, -190.5) * mm});
            skLineSegment(sketch, "E150.4", {"start": v(88.9, -190.5) * mm, "end": v(81.46, -208.46) * mm});
            skLineSegment(sketch, "E150.5", {"start": v(81.46, -208.46) * mm, "end": v(63.5, -215.9) * mm});
            skLineSegment(sketch, "E150.6", {"start": v(63.5, -215.9) * mm, "end": v(45.54, -208.46) * mm});
            skLineSegment(sketch, "E150.7", {"start": v(45.54, -208.46) * mm, "end": v(38.1, -190.5) * mm});
            skSolve(sketch);
        }
        {
            var Q0;
            Q0=makeQuery(id+"F0.imprint","IMPRINT",FACE,{"disambiguationData":[TD([[makeQuery(id+"F0.imprint","IMPRINT",EDGE,{"derivedFrom":sQuery(id+"F0.wireOp",EDGE,"E16.0")}),-1.0]])]});
            var Q1;
            Q1=makeQuery(id+"F0.imprint","IMPRINT",FACE,{"disambiguationData":[TD([[makeQuery(id+"F0.imprint","IMPRINT",EDGE,{"derivedFrom":sQuery(id+"F0.wireOp",EDGE,"E17.0")}),-1.0]])]});
            var Q2;
            Q2=makeQuery(id+"F0.imprint","IMPRINT",FACE,{"disambiguationData":[TD([[makeQuery(id+"F0.imprint","IMPRINT",EDGE,{"derivedFrom":sQuery(id+"F0.wireOp",EDGE,"E23.0")}),-1.0]])]});
            var Q3;
            Q3=makeQuery(id+"F0.imprint","IMPRINT",FACE,{"disambiguationData":[TD([[makeQuery(id+"F0.imprint","IMPRINT",EDGE,{"derivedFrom":sQuery(id+"F0.wireOp",EDGE,"E24.0")}),-1.0]])]});
            var Q4;
            Q4=makeQuery(id+"F0.imprint","IMPRINT",FACE,{"disambiguationData":[TD([[makeQuery(id+"F0.imprint","IMPRINT",EDGE,{"derivedFrom":sQuery(id+"F0.wireOp",EDGE,"E22.0")}),-1.0]])]});
            var Q5;
            Q5=makeQuery(id+"F0.imprint","IMPRINT",FACE,{"disambiguationData":[TD([[makeQuery(id+"F0.imprint","IMPRINT",EDGE,{"derivedFrom":sQuery(id+"F0.wireOp",EDGE,"E18.0")}),-1.0]])]});
            extrude(context, id + "F8", {"entities" : qUnion([Q0, Q1, Q2, Q3, Q4, Q5]), "operationType" : NewBodyOperationType.REMOVE, "oppositeDirection" : true, "depth" : 25.4 * mm, "offsetDistance" : 25.4 * mm, "hasDraft" : true, "draftAngle" : 3 * degree, "draftPullDirection" : true});
        }
        {
            var Q0;
            Q0=makeQuery(id+"F4.imprint","IMPRINT",FACE,{"disambiguationData":[TD([[makeQuery(id+"F4.imprint","IMPRINT",EDGE,{"derivedFrom":sQuery(id+"F4.wireOp",EDGE,"E71.0")}),-1.0]])]});
            extrude(context, id + "F9", {"entities" : qUnion([Q0]), "operationType" : NewBodyOperationType.REMOVE, "oppositeDirection" : true, "depth" : 25.4 * mm, "offsetDistance" : 25.4 * mm, "hasDraft" : true, "draftAngle" : 3 * degree});
        }
        {
            var Q0;
            Q0=makeQuery(id+"F6.imprint","IMPRINT",FACE,{"disambiguationData":[TD([[makeQuery(id+"F6.imprint","IMPRINT",EDGE,{"derivedFrom":sQuery(id+"F6.wireOp",EDGE,"E119.0")}),-1.0]])]});
            var Q1;
            Q1=makeQuery(id+"F6.imprint","IMPRINT",FACE,{"disambiguationData":[TD([[makeQuery(id+"F6.imprint","IMPRINT",EDGE,{"derivedFrom":sQuery(id+"F6.wireOp",EDGE,"E121.0")}),-1.0]])]});
            var Q2;
            Q2=makeQuery(id+"F6.imprint","IMPRINT",FACE,{"disambiguationData":[TD([[makeQuery(id+"F6.imprint","IMPRINT",EDGE,{"derivedFrom":sQuery(id+"F6.wireOp",EDGE,"E123.0")}),-1.0]])]});
            var Q3;
            Q3=makeQuery(id+"F6.imprint","IMPRINT",FACE,{"disambiguationData":[TD([[makeQuery(id+"F6.imprint","IMPRINT",EDGE,{"derivedFrom":sQuery(id+"F6.wireOp",EDGE,"E125.0")}),-1.0]])]});
            var Q4;
            Q4=makeQuery(id+"F6.imprint","IMPRINT",FACE,{"disambiguationData":[TD([[makeQuery(id+"F6.imprint","IMPRINT",EDGE,{"derivedFrom":sQuery(id+"F6.wireOp",EDGE,"E117.0")}),-1.0]])]});
            extrude(context, id + "F10", {"entities" : qUnion([Q0, Q1, Q2, Q3, Q4]), "operationType" : NewBodyOperationType.REMOVE, "oppositeDirection" : true, "depth" : 25.4 * mm, "offsetDistance" : 25.4 * mm, "hasDraft" : true, "draftAngle" : 3 * degree});
        }
        {
            var Q0;
            Q0=makeQuery(id+"F7.imprint","IMPRINT",FACE,{"disambiguationData":[TD([[makeQuery(id+"F7.imprint","IMPRINT",EDGE,{"derivedFrom":sQuery(id+"F7.wireOp",EDGE,"E142.0")}),-1.0]])]});
            var Q1;
            Q1=makeQuery(id+"F7.imprint","IMPRINT",FACE,{"disambiguationData":[TD([[makeQuery(id+"F7.imprint","IMPRINT",EDGE,{"derivedFrom":sQuery(id+"F7.wireOp",EDGE,"E148.0")}),-1.0]])]});
            var Q2;
            Q2=makeQuery(id+"F7.imprint","IMPRINT",FACE,{"disambiguationData":[TD([[makeQuery(id+"F7.imprint","IMPRINT",EDGE,{"derivedFrom":sQuery(id+"F7.wireOp",EDGE,"E150.0")}),-1.0]])]});
            var Q3;
            Q3=makeQuery(id+"F7.imprint","IMPRINT",FACE,{"disambiguationData":[TD([[makeQuery(id+"F7.imprint","IMPRINT",EDGE,{"derivedFrom":sQuery(id+"F7.wireOp",EDGE,"E144.0")}),-1.0]])]});
            extrude(context, id + "F11", {"entities" : qUnion([Q0, Q1, Q2, Q3]), "operationType" : NewBodyOperationType.REMOVE, "oppositeDirection" : true, "depth" : 25.4 * mm, "offsetDistance" : 25.4 * mm, "hasDraft" : true, "draftAngle" : 3 * degree});
        }
        {
            var Q0;
            Q0=makeQuery(id+"F3.imprint","IMPRINT",FACE,{"disambiguationData":[TD([[makeQuery(id+"F3.imprint","IMPRINT",EDGE,{"derivedFrom":sQuery(id+"F3.wireOp",EDGE,"E42.0")}),-1.0]])]});
            var Q1;
            Q1=makeQuery(id+"F3.imprint","IMPRINT",FACE,{"disambiguationData":[TD([[makeQuery(id+"F3.imprint","IMPRINT",EDGE,{"derivedFrom":sQuery(id+"F3.wireOp",EDGE,"E50.0")}),-1.0]])]});
            extrude(context, id + "F12", {"entities" : qUnion([Q0, Q1]), "operationType" : NewBodyOperationType.REMOVE, "oppositeDirection" : true, "depth" : 25.4 * mm, "offsetDistance" : 25.4 * mm, "hasDraft" : true, "draftAngle" : 3 * degree});
        }
        {
            var Q0;
            Q0=makeQuery(id+"F5.imprint","IMPRINT",FACE,{"disambiguationData":[TD([[makeQuery(id+"F5.imprint","IMPRINT",EDGE,{"derivedFrom":sQuery(id+"F5.wireOp",EDGE,"E92.0")}),-1.0]])]});
            var Q1;
            Q1=makeQuery(id+"F5.imprint","IMPRINT",FACE,{"disambiguationData":[TD([[makeQuery(id+"F5.imprint","IMPRINT",EDGE,{"derivedFrom":sQuery(id+"F5.wireOp",EDGE,"E96.0")}),-1.0]])]});
            var Q2;
            Q2=makeQuery(id+"F5.imprint","IMPRINT",FACE,{"disambiguationData":[TD([[makeQuery(id+"F5.imprint","IMPRINT",EDGE,{"derivedFrom":sQuery(id+"F5.wireOp",EDGE,"E100.0")}),-1.0]])]});
            extrude(context, id + "F13", {"entities" : qUnion([Q0, Q1, Q2]), "operationType" : NewBodyOperationType.REMOVE, "oppositeDirection" : true, "depth" : 25.4 * mm, "offsetDistance" : 25.4 * mm, "hasDraft" : true, "draftAngle" : 3 * degree});
        }
        {
            var Q0;
            Q0=makeQuery(id+"F2.opExtrude","CAP_EDGE",EDGE,{"disambiguationData":[OSD([sQuery(id+"F1.wireOp",EDGE,"E25.right")])],"isStart":true});
            var Q1;
            Q1=makeQuery(id+"F2.opExtrude","SWEPT_EDGE",EDGE,{"disambiguationData":[OSD([sQuery(id+"F1.wireOp",EDGE,"E25.bottom"),sQuery(id+"F1.wireOp",EDGE,"E25.right")])]});
            var Q2;
            Q2=makeQuery(id+"F2.opExtrude","CAP_EDGE",EDGE,{"disambiguationData":[OSD([sQuery(id+"F1.wireOp",EDGE,"E25.right")])],"isStart":false});
            var Q3;
            Q3=makeQuery(id+"F2.opExtrude","SWEPT_EDGE",EDGE,{"disambiguationData":[OSD([sQuery(id+"F1.wireOp",EDGE,"E25.top"),sQuery(id+"F1.wireOp",EDGE,"E25.right")])]});
            var Q4;
            Q4=makeQuery(id+"F2.opExtrude","CAP_EDGE",EDGE,{"disambiguationData":[OSD([sQuery(id+"F1.wireOp",EDGE,"E25.top")])],"isStart":false});
            var Q5;
            Q5=makeQuery(id+"F2.opExtrude","CAP_EDGE",EDGE,{"disambiguationData":[OSD([sQuery(id+"F1.wireOp",EDGE,"E25.bottom")])],"isStart":false});
            var Q6;
            Q6=makeQuery(id+"F2.opExtrude","CAP_EDGE",EDGE,{"disambiguationData":[OSD([sQuery(id+"F1.wireOp",EDGE,"E25.left")])],"isStart":false});
            var Q7;
            Q7=makeQuery(id+"F2.opExtrude","CAP_EDGE",EDGE,{"disambiguationData":[OSD([sQuery(id+"F1.wireOp",EDGE,"E25.left")])],"isStart":true});
            var Q8;
            Q8=makeQuery(id+"F2.opExtrude","SWEPT_EDGE",EDGE,{"disambiguationData":[OSD([sQuery(id+"F1.wireOp",EDGE,"E25.bottom"),sQuery(id+"F1.wireOp",EDGE,"E25.left")])]});
            var Q9;
            Q9=makeQuery(id+"F2.opExtrude","CAP_EDGE",EDGE,{"disambiguationData":[OSD([sQuery(id+"F1.wireOp",EDGE,"E25.bottom")])],"isStart":true});
            var Q10;
            Q10=makeQuery(id+"F2.opExtrude","SWEPT_EDGE",EDGE,{"disambiguationData":[OSD([sQuery(id+"F1.wireOp",EDGE,"E25.top"),sQuery(id+"F1.wireOp",EDGE,"E25.left")])]});
            var Q11;
            Q11=makeQuery(id+"F2.opExtrude","CAP_EDGE",EDGE,{"disambiguationData":[OSD([sQuery(id+"F1.wireOp",EDGE,"E25.top")])],"isStart":true});
            fillet(context, id + "F14", {"entities" : qUnion([Q0, Q1, Q2, Q3, Q4, Q5, Q6, Q7, Q8, Q9, Q10, Q11]), "radius" : 12.7 * mm, "rho" : 0.5, "crossSection" : FilletCrossSection.CONIC, "allowEdgeOverflow" : false});
        }
        {
            var Q0;
            Q0=qCreatedBy(makeId("Front.planeOp"),FACE);
            var Q1;
            Q1 = qBodyType(qCreatedBy(id + "F16" ,EDGE), BodyType.WIRE);
            cPlane(context, id + "F15", {"entities" : qUnion([Q0, Q1]), "cplaneType" : CPlaneType.OFFSET, "offset" : 127 * mm, "oppositeDirection" : true, "width" : 152.4 * mm, "height" : 152.4 * mm});
        }
        {
            var Q0;
            Q0=qCreatedBy(id+"F15.planeOp",FACE);
            var sketch = newSketch(context, id + "F16", { "sketchPlane" : qUnion([Q0])});
            skPoint(sketch, "E151.middle", {"position": v(0, 0) * mm});
            skPoint(sketch, "E151.right.end.orphan", {"position": v(50.8, 50.8) * mm});
            skPoint(sketch, "E152.orphan", {"position": v(50.8, -50.8) * mm});
            skPoint(sketch, "E151.left.end.orphan", {"position": v(-50.8, 50.8) * mm});
            skPoint(sketch, "E151.bottom.start.orphan", {"position": v(-50.8, -50.8) * mm});
            skCircle(sketch, "E153", {"center": v(0, 0) * mm, "radius": 88.9 * mm});
            skLineSegment(sketch, "E154", {"start": v(-4.6, 88.78) * mm, "end": v(3.45, -88.83) * mm});
            skSolve(sketch);
        }
        {
            var Q0;
            {var subQ0=sQuery(id+"F16.wireOp",EDGE,"E154");Q0=makeQuery(id+"F16.imprint","IMPRINT",FACE,{"disambiguationData":[TD([[makeQuery(id+"F16.imprint","IMPRINT",EDGE,{"derivedFrom":subQ0}),1.0]])]});}
            var Q1;
            Q1=sQuery(id+"F16.wireOp",EDGE,"E154");
            revolve(context, id + "F17", {"operationType" : NewBodyOperationType.REMOVE, "surfaceOperationType" : NewSurfaceOperationType.NEW, "entities" : qUnion([Q0]), "axis" : qUnion([Q1]), "revolveType" : RevolveType.FULL});
        }
    });
